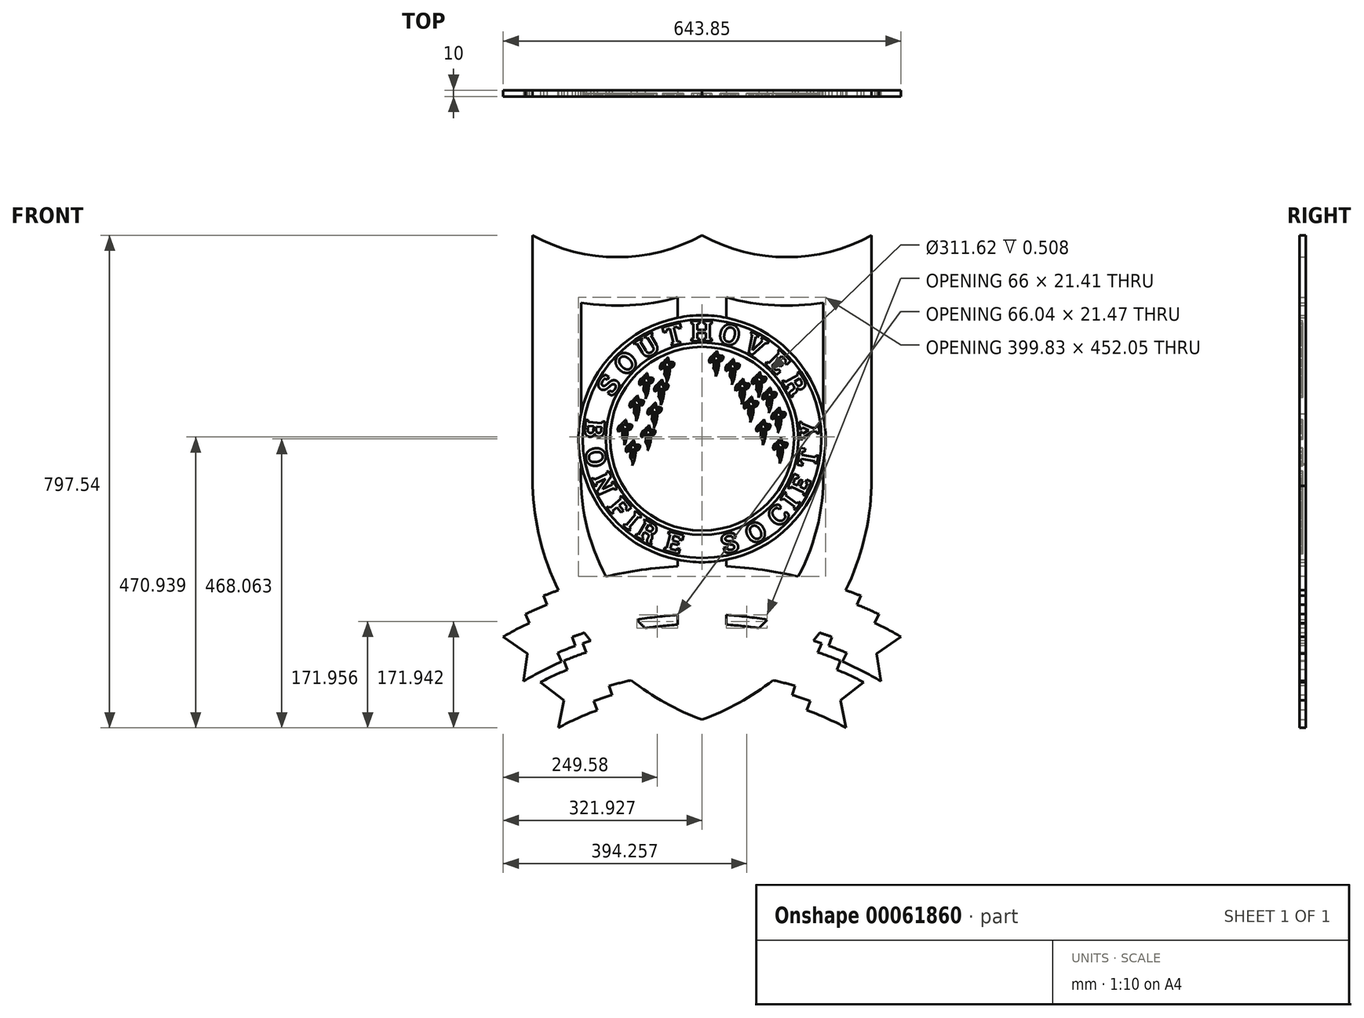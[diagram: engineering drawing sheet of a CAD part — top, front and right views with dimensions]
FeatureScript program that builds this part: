
annotation { "Feature Type Name" : "Feature", "Feature Type Description" : "" }
export const myFeature = defineFeature(function(context is Context, id is Id, definition is map)
    precondition{}
    {
        {
            var Q0;
            Q0=qCreatedBy(makeId("Front.planeOp"),FACE);
            var sketch = newSketch(context, id + "F0", { "sketchPlane" : qUnion([Q0])});
            skCircle(sketch, "E0", {"center": v(6.77, 469.76) * mm, "radius": 199.91 * mm});
            skSolve(sketch);
        }
        {
            var Q0;
            Q0 = qSketchRegion(id + "F0", true);
            extrude(context, id + "F1", {"entities" : qUnion([Q0]), "depth" : 10 * mm, "offsetDistance" : 25.4 * mm});
        }
        {
            var Q0;
            Q0=qCreatedBy(makeId("Front.planeOp"),FACE);
            var sketch = newSketch(context, id + "F2", { "sketchPlane" : qUnion([Q0])});
            skArc(sketch, "E1", {"start": v(-267.62, 799.24) * mm, "mid": v(-130.38, 764) * mm, "end": v(6.86, 799.22) * mm});
            skArc(sketch, "E2", {"start": v(-189.02, 690.2) * mm, "mid": v(-110.33, 685.87) * mm, "end": v(-32.56, 698.67) * mm});
            skArc(sketch, "E3", {"start": v(-189.02, 427.97) * mm, "mid": v(-152.25, 253.46) * mm, "end": v(-32.56, 121.24) * mm});
            skArc(sketch, "E4.0", {"start": v(-189.02, 510.16) * mm, "mid": v(-193.15, 469.76) * mm, "end": v(-189.02, 429.36) * mm});
            skLineSegment(sketch, "E5", {"start": v(6.77, 469.76) * mm, "end": v(-343.44, 469.76) * mm, "construction": true});
            skLineSegment(sketch, "E6", {"start": v(-343.44, 469.76) * mm, "end": v(6.77, -66.3) * mm, "construction": true});
            skLineSegment(sketch, "E7", {"start": v(6.77, -66.3) * mm, "end": v(6.77, 469.76) * mm, "construction": true});
            skLineSegment(sketch, "E8", {"start": v(-267.62, 799.24) * mm, "end": v(-267.62, 393.65) * mm});
            skArc(sketch, "E9", {"start": v(-267.62, 393.65) * mm, "mid": v(-188.5, 162.16) * mm, "end": v(6.77, 14.8) * mm});
            skLineSegment(sketch, "E10", {"start": v(-32.56, 698.67) * mm, "end": v(-32.56, 665.77) * mm});
            skLineSegment(sketch, "E11", {"start": v(-189.02, 690.2) * mm, "end": v(-189.02, 510.16) * mm});
            skArc(sketch, "E12.MirrorCS", {"start": v(281.15, 799.24) * mm, "mid": v(143.92, 764) * mm, "end": v(6.68, 799.22) * mm});
            skLineSegment(sketch, "E13.MirrorCS", {"start": v(281.15, 799.24) * mm, "end": v(281.15, 393.65) * mm});
            skArc(sketch, "E14.MirrorCS", {"start": v(202.56, 690.2) * mm, "mid": v(123.86, 685.87) * mm, "end": v(46.1, 698.67) * mm});
            skLineSegment(sketch, "E15.MirrorCS", {"start": v(202.56, 690.2) * mm, "end": v(202.56, 510.16) * mm});
            skLineSegment(sketch, "E16.MirrorCS", {"start": v(46.1, 698.67) * mm, "end": v(46.1, 665.77) * mm});
            skArc(sketch, "E17.MirrorCS", {"start": v(202.56, 427.97) * mm, "mid": v(165.79, 253.46) * mm, "end": v(46.1, 121.24) * mm});
            skArc(sketch, "E18.MirrorCS", {"start": v(281.15, 393.65) * mm, "mid": v(202.03, 162.16) * mm, "end": v(6.77, 14.8) * mm});
            skLineSegment(sketch, "E19.trimOffspring", {"start": v(-32.56, 273.76) * mm, "end": v(-32.56, 121.24) * mm});
            skLineSegment(sketch, "E20.trimOffspring", {"start": v(-189.02, 429.36) * mm, "end": v(-189.02, 427.97) * mm});
            skArc(sketch, "E21.trimOffspring", {"start": v(-32.56, 273.76) * mm, "mid": v(6.77, 269.85) * mm, "end": v(46.1, 273.76) * mm});
            skLineSegment(sketch, "E22.trimOffspring", {"start": v(46.1, 273.76) * mm, "end": v(46.1, 121.24) * mm});
            skArc(sketch, "E23.trimOffspring", {"start": v(202.56, 429.36) * mm, "mid": v(206.68, 469.76) * mm, "end": v(202.56, 510.16) * mm});
            skLineSegment(sketch, "E24.trimOffspring", {"start": v(202.56, 429.36) * mm, "end": v(202.56, 427.97) * mm});
            skArc(sketch, "E25.trimOffspring", {"start": v(46.1, 665.77) * mm, "mid": v(6.77, 669.68) * mm, "end": v(-32.56, 665.77) * mm});
            skSolve(sketch);
        }
        {
            var Q0;
            Q0 = qSketchRegion(id + "F2", true);
            extrude(context, id + "F3", {"entities" : qUnion([Q0]), "depth" : 10 * mm, "offsetDistance" : 25.4 * mm});
        }
        {
            var Q0;
            Q0=makeQuery(id+"F3.opExtrude","CAP_FACE",FACE,{"disambiguationData":[OSD([sQuery(id+"F2.wireOp",EDGE,"E1"),sQuery(id+"F2.wireOp",EDGE,"E2"),sQuery(id+"F2.wireOp",EDGE,"E3"),sQuery(id+"F2.wireOp",EDGE,"E8"),sQuery(id+"F2.wireOp",EDGE,"E9"),sQuery(id+"F2.wireOp",EDGE,"E10"),sQuery(id+"F2.wireOp",EDGE,"E11"),sQuery(id+"F2.wireOp",EDGE,"E12.MirrorCS"),sQuery(id+"F2.wireOp",EDGE,"E13.MirrorCS"),sQuery(id+"F2.wireOp",EDGE,"E14.MirrorCS"),sQuery(id+"F2.wireOp",EDGE,"E15.MirrorCS"),sQuery(id+"F2.wireOp",EDGE,"E16.MirrorCS"),sQuery(id+"F2.wireOp",EDGE,"E17.MirrorCS"),sQuery(id+"F2.wireOp",EDGE,"E18.MirrorCS")])],"isStart":false});
            var sketch = newSketch(context, id + "F4", { "sketchPlane" : qUnion([Q0])});
            skCircle(sketch, "E26.0", {"center": v(6.77, 469.76) * mm, "radius": 199.91 * mm, "construction": true});
            skLineSegment(sketch, "E27", {"start": v(6.77, 469.76) * mm, "end": v(6.77, 811.35) * mm, "construction": true});
            skArc(sketch, "E28", {"start": v(-8.6, 766.76) * mm, "mid": v(-16.65, 759.4) * mm, "end": v(-8.5, 752.14) * mm});
            skArc(sketch, "E29", {"start": v(-4.77, 746.9) * mm, "mid": v(-8.07, 738.78) * mm, "end": v(0.3, 736.11) * mm});
            skArc(sketch, "E30", {"start": v(2.95, 733.33) * mm, "mid": v(2.82, 728.75) * mm, "end": v(6.77, 726.42) * mm});
            skArc(sketch, "E31", {"start": v(-9.15, 782.05) * mm, "mid": v(-13.27, 776.66) * mm, "end": v(-8.73, 771.63) * mm});
            skArc(sketch, "E32", {"start": v(-9.15, 782.05) * mm, "mid": v(1.37, 788.5) * mm, "end": v(5.88, 800) * mm});
            skArc(sketch, "E33", {"start": v(2.95, 733.33) * mm, "mid": v(2.7, 735.76) * mm, "end": v(0.3, 736.11) * mm});
            skArc(sketch, "E34", {"start": v(-4.77, 746.9) * mm, "mid": v(-3.83, 747.3) * mm, "end": v(-2.92, 747.75) * mm});
            skArc(sketch, "E35", {"start": v(-8.5, 752.14) * mm, "mid": v(-6.95, 752.43) * mm, "end": v(-5.47, 752.96) * mm});
            skArc(sketch, "E36", {"start": v(-8.6, 766.76) * mm, "mid": v(-7.07, 766.64) * mm, "end": v(-5.54, 766.59) * mm});
            skArc(sketch, "E37", {"start": v(-8.73, 771.63) * mm, "mid": v(-7.17, 771.47) * mm, "end": v(-5.61, 771.46) * mm});
            skArc(sketch, "E38", {"start": v(-2.92, 747.75) * mm, "mid": v(-1.7, 751.58) * mm, "end": v(-5.47, 752.96) * mm});
            skArc(sketch, "E39", {"start": v(-5.54, 766.59) * mm, "mid": v(-3.07, 769.06) * mm, "end": v(-5.61, 771.46) * mm});
            skArc(sketch, "E40.0", {"start": v(-8.76, 780.32) * mm, "mid": v(0.95, 785.48) * mm, "end": v(6.77, 794.8) * mm});
            skLineSegment(sketch, "E41.0", {"start": v(7.66, 800) * mm, "end": v(5.88, 800) * mm});
            skPoint(sketch, "E42.orphan", {"position": v(-268.66, 800) * mm});
            skPoint(sketch, "E43.orphan", {"position": v(282.43, 800) * mm});
            skArc(sketch, "E44.0", {"start": v(-8.47, 773.39) * mm, "mid": v(-7.08, 773.25) * mm, "end": v(-5.68, 773.24) * mm});
            skArc(sketch, "E44.1", {"start": v(-5.57, 764.81) * mm, "mid": v(-1.3, 769.08) * mm, "end": v(-5.68, 773.24) * mm});
            skArc(sketch, "E44.2", {"start": v(-8.76, 764.99) * mm, "mid": v(-7.17, 764.86) * mm, "end": v(-5.57, 764.81) * mm});
            skArc(sketch, "E45.0", {"start": v(-5.54, 744.78) * mm, "mid": v(-3.76, 745.39) * mm, "end": v(-2.07, 746.19) * mm});
            skArc(sketch, "E45.1", {"start": v(-2.07, 746.19) * mm, "mid": v(-0.1, 752.36) * mm, "end": v(-6.19, 754.58) * mm});
            skArc(sketch, "E45.2", {"start": v(-8.7, 753.91) * mm, "mid": v(-7.42, 754.15) * mm, "end": v(-6.19, 754.58) * mm});
            skArc(sketch, "E46.0", {"start": v(4.46, 732.38) * mm, "mid": v(4, 736.99) * mm, "end": v(-0.59, 737.66) * mm});
            skArc(sketch, "E47.0", {"start": v(4.46, 732.38) * mm, "mid": v(4.38, 729.6) * mm, "end": v(6.77, 728.2) * mm});
            skArc(sketch, "E48.0", {"start": v(-4.14, 745.24) * mm, "mid": v(-6.46, 739.53) * mm, "end": v(-0.59, 737.66) * mm});
            skArc(sketch, "E49.0", {"start": v(-8.76, 780.32) * mm, "mid": v(-11.5, 776.73) * mm, "end": v(-8.47, 773.39) * mm});
            skArc(sketch, "E50.0", {"start": v(-8.76, 764.99) * mm, "mid": v(-14.87, 759.4) * mm, "end": v(-8.7, 753.91) * mm});
            skLineSegment(sketch, "E51.MirrorCS", {"start": v(5.88, 800) * mm, "end": v(5.88, 800) * mm});
            skArc(sketch, "E52.MirrorCS", {"start": v(22.13, 766.76) * mm, "mid": v(20.6, 766.64) * mm, "end": v(19.08, 766.59) * mm});
            skArc(sketch, "E53.MirrorCS", {"start": v(22, 773.39) * mm, "mid": v(20.62, 773.25) * mm, "end": v(19.22, 773.24) * mm});
            skArc(sketch, "E54.MirrorCS", {"start": v(22.03, 752.14) * mm, "mid": v(20.49, 752.43) * mm, "end": v(19, 752.96) * mm});
            skArc(sketch, "E55.MirrorCS", {"start": v(22.3, 764.99) * mm, "mid": v(20.7, 764.86) * mm, "end": v(19.1, 764.81) * mm});
            skArc(sketch, "E56.MirrorCS", {"start": v(18.3, 746.9) * mm, "mid": v(17.36, 747.3) * mm, "end": v(16.45, 747.75) * mm});
            skArc(sketch, "E57.MirrorCS", {"start": v(22.23, 753.91) * mm, "mid": v(20.95, 754.15) * mm, "end": v(19.72, 754.58) * mm});
            skArc(sketch, "E58.MirrorCS", {"start": v(22.26, 771.63) * mm, "mid": v(20.7, 771.47) * mm, "end": v(19.15, 771.46) * mm});
            skArc(sketch, "E59.MirrorCS", {"start": v(9.08, 732.38) * mm, "mid": v(9.16, 729.6) * mm, "end": v(6.77, 728.2) * mm});
            skArc(sketch, "E60.MirrorCS", {"start": v(10.58, 733.33) * mm, "mid": v(10.83, 735.76) * mm, "end": v(13.24, 736.11) * mm});
            skArc(sketch, "E61.MirrorCS", {"start": v(19.07, 744.78) * mm, "mid": v(17.3, 745.39) * mm, "end": v(15.6, 746.19) * mm});
            skArc(sketch, "E62.MirrorCS", {"start": v(19.08, 766.59) * mm, "mid": v(16.6, 769.06) * mm, "end": v(19.15, 771.46) * mm});
            skArc(sketch, "E63.MirrorCS", {"start": v(22.3, 780.32) * mm, "mid": v(12.58, 785.48) * mm, "end": v(6.77, 794.8) * mm});
            skArc(sketch, "E64.MirrorCS", {"start": v(16.45, 747.75) * mm, "mid": v(15.24, 751.58) * mm, "end": v(19, 752.96) * mm});
            skArc(sketch, "E65.MirrorCS", {"start": v(9.08, 732.38) * mm, "mid": v(9.54, 736.99) * mm, "end": v(14.12, 737.66) * mm});
            skArc(sketch, "E66.MirrorCS", {"start": v(22.3, 764.99) * mm, "mid": v(28.4, 759.4) * mm, "end": v(22.23, 753.91) * mm});
            skArc(sketch, "E67.MirrorCS", {"start": v(22.69, 782.05) * mm, "mid": v(12.16, 788.5) * mm, "end": v(7.66, 800) * mm});
            skArc(sketch, "E68.MirrorCS", {"start": v(10.58, 733.33) * mm, "mid": v(10.71, 728.75) * mm, "end": v(6.77, 726.42) * mm});
            skArc(sketch, "E69.MirrorCS", {"start": v(17.67, 745.24) * mm, "mid": v(20, 739.53) * mm, "end": v(14.12, 737.66) * mm});
            skArc(sketch, "E70.MirrorCS", {"start": v(18.3, 746.9) * mm, "mid": v(21.6, 738.78) * mm, "end": v(13.24, 736.11) * mm});
            skArc(sketch, "E71.MirrorCS", {"start": v(22.69, 782.05) * mm, "mid": v(26.8, 776.66) * mm, "end": v(22.26, 771.63) * mm});
            skArc(sketch, "E72.MirrorCS", {"start": v(22.13, 766.76) * mm, "mid": v(30.18, 759.4) * mm, "end": v(22.03, 752.14) * mm});
            skArc(sketch, "E73.MirrorCS", {"start": v(22.3, 780.32) * mm, "mid": v(25.03, 776.73) * mm, "end": v(22, 773.39) * mm});
            skArc(sketch, "E74.MirrorCS", {"start": v(19.1, 764.81) * mm, "mid": v(14.83, 769.08) * mm, "end": v(19.22, 773.24) * mm});
            skArc(sketch, "E75.MirrorCS", {"start": v(15.6, 746.19) * mm, "mid": v(13.64, 752.36) * mm, "end": v(19.72, 754.58) * mm});
            skArc(sketch, "E76.trimOffspring", {"start": v(5.88, 799.98) * mm, "mid": v(5.88, 799.99) * mm, "end": v(5.88, 800) * mm});
            skArc(sketch, "E77.trimOffspring", {"start": v(7.66, 799.98) * mm, "mid": v(7.66, 799.99) * mm, "end": v(7.66, 800) * mm});
            skArc(sketch, "E78", {"start": v(6.77, 739.23) * mm, "mid": v(7.13, 743.58) * mm, "end": v(7.42, 747.94) * mm});
            skArc(sketch, "E79", {"start": v(6.99, 782.56) * mm, "mid": v(13.75, 778.46) * mm, "end": v(21.5, 776.88) * mm});
            skArc(sketch, "E80", {"start": v(7.12, 780.88) * mm, "mid": v(13.95, 777.58) * mm, "end": v(21.5, 776.88) * mm});
            skArc(sketch, "E81", {"start": v(7.82, 764.42) * mm, "mid": v(14.94, 760.75) * mm, "end": v(22.84, 759.45) * mm});
            skArc(sketch, "E82", {"start": v(7.83, 762.95) * mm, "mid": v(15.05, 759.97) * mm, "end": v(22.84, 759.45) * mm});
            skArc(sketch, "E83", {"start": v(7.49, 749.17) * mm, "mid": v(10.93, 744.23) * mm, "end": v(16.2, 741.31) * mm});
            skArc(sketch, "E84", {"start": v(7.42, 747.94) * mm, "mid": v(10.85, 743.37) * mm, "end": v(16.2, 741.31) * mm});
            skPoint(sketch, "E85.MirrorCS.end.orphan", {"position": v(6.77, 785.08) * mm});
            skPoint(sketch, "E85.MirrorCS.start.orphan", {"position": v(6.77, 739.23) * mm});
            skArc(sketch, "E86.trimOffspring", {"start": v(6.99, 782.56) * mm, "mid": v(6.88, 783.82) * mm, "end": v(6.77, 785.08) * mm});
            skArc(sketch, "E87.trimOffspring", {"start": v(7.82, 764.42) * mm, "mid": v(7.6, 772.66) * mm, "end": v(7.12, 780.88) * mm});
            skArc(sketch, "E88.trimOffspring", {"start": v(7.49, 749.17) * mm, "mid": v(7.75, 756.06) * mm, "end": v(7.83, 762.95) * mm});
            skArc(sketch, "E89.MirrorCS", {"start": v(6.55, 782.56) * mm, "mid": v(-0.22, 778.46) * mm, "end": v(-7.97, 776.88) * mm});
            skArc(sketch, "E90.MirrorCS", {"start": v(6.41, 780.88) * mm, "mid": v(-0.41, 777.58) * mm, "end": v(-7.97, 776.88) * mm});
            skArc(sketch, "E91.MirrorCS", {"start": v(5.72, 764.42) * mm, "mid": v(5.93, 772.66) * mm, "end": v(6.41, 780.88) * mm});
            skArc(sketch, "E92.MirrorCS", {"start": v(6.55, 782.56) * mm, "mid": v(6.65, 783.82) * mm, "end": v(6.77, 785.08) * mm});
            skArc(sketch, "E93.MirrorCS", {"start": v(5.7, 762.95) * mm, "mid": v(-1.51, 759.97) * mm, "end": v(-9.3, 759.45) * mm});
            skArc(sketch, "E94.MirrorCS", {"start": v(6.05, 749.17) * mm, "mid": v(5.78, 756.06) * mm, "end": v(5.7, 762.95) * mm});
            skArc(sketch, "E95.MirrorCS", {"start": v(5.72, 764.42) * mm, "mid": v(-1.4, 760.75) * mm, "end": v(-9.3, 759.45) * mm});
            skArc(sketch, "E96.MirrorCS", {"start": v(6.05, 749.17) * mm, "mid": v(2.6, 744.23) * mm, "end": v(-2.66, 741.31) * mm});
            skArc(sketch, "E97.MirrorCS", {"start": v(6.11, 747.94) * mm, "mid": v(2.68, 743.37) * mm, "end": v(-2.66, 741.31) * mm});
            skArc(sketch, "E98.MirrorCS", {"start": v(6.77, 739.23) * mm, "mid": v(6.4, 743.58) * mm, "end": v(6.11, 747.94) * mm});
            skSolve(sketch);
        }
        {
            var Q0;
            {var subQ151=sQuery(id+"F2.wireOp",EDGE,"E1");var subQ170=sQuery(id+"F2.wireOp",EDGE,"E12.MirrorCS");var subQ178=makeQuery(id+"F3.opExtrude","SWEPT_FACE",FACE,{"disambiguationData":[OSD([subQ151])]});var subQ182=sQuery(id+"F2.wireOp",EDGE,"E9");var subQ204=sQuery(id+"F2.wireOp",EDGE,"E3");var subQ205=makeQuery(id+"F3.opExtrude","SWEPT_FACE",FACE,{"disambiguationData":[OSD([subQ204])]});var subQ208=sQuery(id+"F2.wireOp",EDGE,"E2");var subQ209=makeQuery(id+"F3.opExtrude","SWEPT_FACE",FACE,{"disambiguationData":[OSD([subQ208])]});var subQ210=sQuery(id+"F2.wireOp",EDGE,"E10");var subQ568=sQuery(id+"F2.wireOp",EDGE,"E16.MirrorCS");var subQ570=sQuery(id+"F2.wireOp",EDGE,"E17.MirrorCS");var subQ572=sQuery(id+"F2.wireOp",EDGE,"E18.MirrorCS");var subQ581=sQuery(id+"F2.wireOp",EDGE,"E14.MirrorCS");var subQ871=sQuery(id+"F2.wireOp",EDGE,"E15.MirrorCS");var subQ872=sQuery(id+"F2.wireOp",EDGE,"E13.MirrorCS");var subQ873=sQuery(id+"F2.wireOp",EDGE,"E11");var subQ874=sQuery(id+"F2.wireOp",EDGE,"E8");var subQ875=makeQuery(id+"F3.opExtrude","CAP_FACE",FACE,{"disambiguationData":[OSD([subQ151,subQ208,subQ204,subQ874,subQ182,subQ210,subQ873,subQ170,subQ872,subQ581,subQ871,subQ568,subQ570,subQ572])],"isStart":false});Q0=makeQuery(id+"FD2YuUjZby6Q1ET_2.1_10.FR0OegjQK6V7KqL_2.boolean.opBoolean","SPLIT",FACE,{"disambiguationData":[TD([subQ178])],"derivedFrom":makeQuery(id+"FD2YuUjZby6Q1ET_2.0_10.FR0OegjQK6V7KqL_2.boolean.opBoolean","SPLIT",FACE,{"disambiguationData":[TD([subQ178])],"derivedFrom":makeQuery(id+"FD2YuUjZby6Q1ET_2.-1_10.FR0OegjQK6V7KqL_2.boolean.opBoolean","SPLIT",FACE,{"disambiguationData":[TD([subQ178])],"derivedFrom":makeQuery(id+"FD2YuUjZby6Q1ET_2.2_9.FR0OegjQK6V7KqL_2.boolean.opBoolean","SPLIT",FACE,{"disambiguationData":[TD([subQ178])],"derivedFrom":makeQuery(id+"FD2YuUjZby6Q1ET_2.1_9.FR0OegjQK6V7KqL_2.boolean.opBoolean","SPLIT",FACE,{"disambiguationData":[TD([subQ178])],"derivedFrom":makeQuery(id+"FD2YuUjZby6Q1ET_2.0_9.FR0OegjQK6V7KqL_2.boolean.opBoolean","SPLIT",FACE,{"disambiguationData":[TD([subQ178])],"derivedFrom":makeQuery(id+"FD2YuUjZby6Q1ET_2.-1_9.FR0OegjQK6V7KqL_2.boolean.opBoolean","SPLIT",FACE,{"disambiguationData":[TD([subQ178])],"derivedFrom":makeQuery(id+"FD2YuUjZby6Q1ET_2.-2_9.FR0OegjQK6V7KqL_2.boolean.opBoolean","SPLIT",FACE,{"disambiguationData":[TD([subQ178])],"derivedFrom":makeQuery(id+"FD2YuUjZby6Q1ET_2.3_8.FR0OegjQK6V7KqL_2.boolean.opBoolean","SPLIT",FACE,{"disambiguationData":[TD([subQ209])],"derivedFrom":makeQuery(id+"FD2YuUjZby6Q1ET_2.2_8.FR0OegjQK6V7KqL_2.boolean.opBoolean","SPLIT",FACE,{"disambiguationData":[TD([subQ178])],"derivedFrom":makeQuery(id+"FD2YuUjZby6Q1ET_2.0_8.FR0OegjQK6V7KqL_2.boolean.opBoolean","SPLIT",FACE,{"disambiguationData":[TD([subQ178])],"derivedFrom":makeQuery(id+"FD2YuUjZby6Q1ET_2.-2_8.FR0OegjQK6V7KqL_2.boolean.opBoolean","SPLIT",FACE,{"disambiguationData":[TD([subQ178])],"derivedFrom":makeQuery(id+"FD2YuUjZby6Q1ET_2.-3_8.FR0OegjQK6V7KqL_2.boolean.opBoolean","SPLIT",FACE,{"disambiguationData":[TD([subQ178])],"derivedFrom":makeQuery(id+"FD2YuUjZby6Q1ET_2.4_7.FR0OegjQK6V7KqL_2.boolean.opBoolean","SPLIT",FACE,{"disambiguationData":[TD([subQ178])],"derivedFrom":makeQuery(id+"FD2YuUjZby6Q1ET_2.3_7.FR0OegjQK6V7KqL_2.boolean.opBoolean","SPLIT",FACE,{"disambiguationData":[TD([subQ178])],"derivedFrom":makeQuery(id+"FD2YuUjZby6Q1ET_2.0_7.FR0OegjQK6V7KqL_2.boolean.opBoolean","SPLIT",FACE,{"disambiguationData":[TD([subQ178])],"derivedFrom":makeQuery(id+"FD2YuUjZby6Q1ET_2.-3_7.FR0OegjQK6V7KqL_2.boolean.opBoolean","SPLIT",FACE,{"disambiguationData":[TD([subQ178])],"derivedFrom":makeQuery(id+"FD2YuUjZby6Q1ET_2.-4_7.FR0OegjQK6V7KqL_2.boolean.opBoolean","SPLIT",FACE,{"disambiguationData":[TD([subQ178])],"derivedFrom":makeQuery(id+"FD2YuUjZby6Q1ET_2.4_6.FR0OegjQK6V7KqL_2.boolean.opBoolean","SPLIT",FACE,{"disambiguationData":[TD([subQ209])],"derivedFrom":makeQuery(id+"FD2YuUjZby6Q1ET_2.3_6.FR0OegjQK6V7KqL_2.boolean.opBoolean","SPLIT",FACE,{"disambiguationData":[TD([subQ178])],"derivedFrom":makeQuery(id+"FD2YuUjZby6Q1ET_2.0_6.FR0OegjQK6V7KqL_2.boolean.opBoolean","SPLIT",FACE,{"disambiguationData":[TD([subQ178])],"derivedFrom":makeQuery(id+"FD2YuUjZby6Q1ET_2.-3_6.FR0OegjQK6V7KqL_2.boolean.opBoolean","SPLIT",FACE,{"disambiguationData":[TD([subQ178])],"derivedFrom":makeQuery(id+"FD2YuUjZby6Q1ET_2.-4_6.FR0OegjQK6V7KqL_2.boolean.opBoolean","SPLIT",FACE,{"disambiguationData":[TD([subQ178])],"derivedFrom":makeQuery(id+"FD2YuUjZby6Q1ET_2.4_5.FR0OegjQK6V7KqL_2.boolean.opBoolean","SPLIT",FACE,{"disambiguationData":[TD([subQ178])],"derivedFrom":makeQuery(id+"FD2YuUjZby6Q1ET_2.3_5.FR0OegjQK6V7KqL_2.boolean.opBoolean","SPLIT",FACE,{"disambiguationData":[TD([subQ178])],"derivedFrom":makeQuery(id+"FD2YuUjZby6Q1ET_2.0_5.FR0OegjQK6V7KqL_2.boolean.opBoolean","SPLIT",FACE,{"disambiguationData":[TD([subQ178])],"derivedFrom":makeQuery(id+"FD2YuUjZby6Q1ET_2.-3_5.FR0OegjQK6V7KqL_2.boolean.opBoolean","SPLIT",FACE,{"disambiguationData":[TD([subQ178])],"derivedFrom":makeQuery(id+"FD2YuUjZby6Q1ET_2.-4_5.FR0OegjQK6V7KqL_2.boolean.opBoolean","SPLIT",FACE,{"disambiguationData":[TD([subQ178])],"derivedFrom":makeQuery(id+"FD2YuUjZby6Q1ET_2.4_4.FR0OegjQK6V7KqL_2.boolean.opBoolean","SPLIT",FACE,{"disambiguationData":[TD([subQ178])],"derivedFrom":makeQuery(id+"FD2YuUjZby6Q1ET_2.3_4.FR0OegjQK6V7KqL_2.boolean.opBoolean","SPLIT",FACE,{"disambiguationData":[TD([subQ178])],"derivedFrom":makeQuery(id+"FD2YuUjZby6Q1ET_2.0_4.FR0OegjQK6V7KqL_2.boolean.opBoolean","SPLIT",FACE,{"disambiguationData":[TD([subQ178])],"derivedFrom":makeQuery(id+"FD2YuUjZby6Q1ET_2.-3_4.FR0OegjQK6V7KqL_2.boolean.opBoolean","SPLIT",FACE,{"disambiguationData":[TD([subQ178])],"derivedFrom":makeQuery(id+"FD2YuUjZby6Q1ET_2.-4_4.FR0OegjQK6V7KqL_2.boolean.opBoolean","SPLIT",FACE,{"disambiguationData":[TD([subQ178])],"derivedFrom":makeQuery(id+"FD2YuUjZby6Q1ET_2.4_3.FR0OegjQK6V7KqL_2.boolean.opBoolean","SPLIT",FACE,{"disambiguationData":[TD([subQ178])],"derivedFrom":makeQuery(id+"FD2YuUjZby6Q1ET_2.3_3.FR0OegjQK6V7KqL_2.boolean.opBoolean","SPLIT",FACE,{"disambiguationData":[TD([subQ178])],"derivedFrom":makeQuery(id+"FD2YuUjZby6Q1ET_2.0_3.FR0OegjQK6V7KqL_2.boolean.opBoolean","SPLIT",FACE,{"disambiguationData":[TD([subQ178])],"derivedFrom":makeQuery(id+"FD2YuUjZby6Q1ET_2.-3_3.FR0OegjQK6V7KqL_2.boolean.opBoolean","SPLIT",FACE,{"disambiguationData":[TD([subQ178])],"derivedFrom":makeQuery(id+"FD2YuUjZby6Q1ET_2.-4_3.FR0OegjQK6V7KqL_2.boolean.opBoolean","SPLIT",FACE,{"disambiguationData":[TD([subQ178])],"derivedFrom":makeQuery(id+"FD2YuUjZby6Q1ET_2.4_2.FR0OegjQK6V7KqL_2.boolean.opBoolean","SPLIT",FACE,{"disambiguationData":[TD([subQ178])],"derivedFrom":makeQuery(id+"FD2YuUjZby6Q1ET_2.3_2.FR0OegjQK6V7KqL_2.boolean.opBoolean","SPLIT",FACE,{"disambiguationData":[TD([subQ178])],"derivedFrom":makeQuery(id+"FD2YuUjZby6Q1ET_2.0_2.FR0OegjQK6V7KqL_2.boolean.opBoolean","SPLIT",FACE,{"disambiguationData":[TD([subQ178])],"derivedFrom":makeQuery(id+"FD2YuUjZby6Q1ET_2.-3_2.FR0OegjQK6V7KqL_2.boolean.opBoolean","SPLIT",FACE,{"disambiguationData":[TD([subQ178])],"derivedFrom":makeQuery(id+"FD2YuUjZby6Q1ET_2.-4_2.FR0OegjQK6V7KqL_2.boolean.opBoolean","SPLIT",FACE,{"disambiguationData":[TD([subQ178])],"derivedFrom":makeQuery(id+"FD2YuUjZby6Q1ET_2.4_1.FR0OegjQK6V7KqL_2.boolean.opBoolean","SPLIT",FACE,{"disambiguationData":[TD([subQ178])],"derivedFrom":makeQuery(id+"FD2YuUjZby6Q1ET_2.3_1.FR0OegjQK6V7KqL_2.boolean.opBoolean","SPLIT",FACE,{"disambiguationData":[TD([subQ205])],"derivedFrom":makeQuery(id+"FD2YuUjZby6Q1ET_2.2_1.FR0OegjQK6V7KqL_2.boolean.opBoolean","SPLIT",FACE,{"disambiguationData":[TD([subQ205])],"derivedFrom":makeQuery(id+"FD2YuUjZby6Q1ET_2.1_1.FR0OegjQK6V7KqL_2.boolean.opBoolean","SPLIT",FACE,{"disambiguationData":[TD([subQ178])],"derivedFrom":makeQuery(id+"FD2YuUjZby6Q1ET_2.0_1.FR0OegjQK6V7KqL_2.boolean.opBoolean","SPLIT",FACE,{"disambiguationData":[TD([subQ178])],"derivedFrom":makeQuery(id+"FD2YuUjZby6Q1ET_2.-1_1.FR0OegjQK6V7KqL_2.boolean.opBoolean","SPLIT",FACE,{"disambiguationData":[TD([subQ178])],"derivedFrom":makeQuery(id+"FD2YuUjZby6Q1ET_2.-2_1.FR0OegjQK6V7KqL_2.boolean.opBoolean","SPLIT",FACE,{"disambiguationData":[TD([subQ178])],"derivedFrom":makeQuery(id+"FD2YuUjZby6Q1ET_2.-3_1.FR0OegjQK6V7KqL_2.boolean.opBoolean","SPLIT",FACE,{"disambiguationData":[TD([subQ178])],"derivedFrom":makeQuery(id+"FD2YuUjZby6Q1ET_2.-4_1.FR0OegjQK6V7KqL_2.boolean.opBoolean","SPLIT",FACE,{"disambiguationData":[TD([subQ178])],"derivedFrom":makeQuery(id+"FD2YuUjZby6Q1ET_2.4.FR0OegjQK6V7KqL_2.boolean.opBoolean","SPLIT",FACE,{"disambiguationData":[TD([subQ209])],"derivedFrom":makeQuery(id+"FD2YuUjZby6Q1ET_2.3.FR0OegjQK6V7KqL_2.boolean.opBoolean","SPLIT",FACE,{"disambiguationData":[TD([subQ209])],"derivedFrom":makeQuery(id+"FD2YuUjZby6Q1ET_2.2.FR0OegjQK6V7KqL_2.boolean.opBoolean","SPLIT",FACE,{"disambiguationData":[TD([subQ209])],"derivedFrom":makeQuery(id+"FD2YuUjZby6Q1ET_2.1.FR0OegjQK6V7KqL_2.boolean.opBoolean","SPLIT",FACE,{"disambiguationData":[TD([subQ209])],"derivedFrom":makeQuery(id+"FD2YuUjZby6Q1ET_2.-1.FR0OegjQK6V7KqL_2.boolean.opBoolean","SPLIT",FACE,{"disambiguationData":[TD([subQ178])],"derivedFrom":makeQuery(id+"FD2YuUjZby6Q1ET_2.-2.FR0OegjQK6V7KqL_2.boolean.opBoolean","SPLIT",FACE,{"disambiguationData":[TD([subQ178])],"derivedFrom":makeQuery(id+"FD2YuUjZby6Q1ET_2.-3.FR0OegjQK6V7KqL_2.boolean.opBoolean","SPLIT",FACE,{"disambiguationData":[TD([subQ178])],"derivedFrom":makeQuery(id+"FD2YuUjZby6Q1ET_2.-4.FR0OegjQK6V7KqL_2.boolean.opBoolean","SPLIT",FACE,{"disambiguationData":[TD([subQ178])],"derivedFrom":makeQuery(id+"FR0OegjQK6V7KqL_2.boolean.opBoolean","SPLIT",FACE,{"disambiguationData":[TD([subQ178])],"derivedFrom":subQ875})})})})})})})})})})})})})})})})})})})})})})})})})})})})})})})})})})})})})})})})})})})})})})})})})})})})})})})})})})})})});}
            var sketch = newSketch(context, id + "F5", { "sketchPlane" : qUnion([Q0])});
            skCircle(sketch, "E99.0", {"center": v(-24.28, 435.37) * mm, "radius": 199.91 * mm, "construction": true});
            skLineSegment(sketch, "E100", {"start": v(-24.28, 435.37) * mm, "end": v(-24.28, 776.96) * mm, "construction": true});
            skArc(sketch, "E101", {"start": v(-39.64, 732.36) * mm, "mid": v(-47.7, 725) * mm, "end": v(-39.54, 717.75) * mm});
            skArc(sketch, "E102", {"start": v(-35.81, 712.51) * mm, "mid": v(-37.73, 711.33) * mm, "end": v(-39.08, 709.53) * mm});
            skArc(sketch, "E103", {"start": v(-28.1, 698.93) * mm, "mid": v(-28.23, 694.35) * mm, "end": v(-24.28, 692.02) * mm});
            skArc(sketch, "E104", {"start": v(-40.2, 747.65) * mm, "mid": v(-41.55, 747.14) * mm, "end": v(-42.72, 746.28) * mm});
            skArc(sketch, "E105", {"start": v(-40.2, 747.65) * mm, "mid": v(-29.67, 754.1) * mm, "end": v(-25.17, 765.6) * mm});
            skArc(sketch, "E106", {"start": v(-28.1, 698.93) * mm, "mid": v(-28.34, 701.36) * mm, "end": v(-30.76, 701.72) * mm});
            skArc(sketch, "E107", {"start": v(-35.81, 712.51) * mm, "mid": v(-34.88, 712.9) * mm, "end": v(-33.97, 713.36) * mm});
            skArc(sketch, "E108", {"start": v(-39.54, 717.75) * mm, "mid": v(-38, 718.04) * mm, "end": v(-36.52, 718.56) * mm});
            skArc(sketch, "E109", {"start": v(-39.64, 732.36) * mm, "mid": v(-38.12, 732.24) * mm, "end": v(-36.6, 732.2) * mm});
            skArc(sketch, "E110", {"start": v(-39.78, 737.23) * mm, "mid": v(-38.22, 737.08) * mm, "end": v(-36.66, 737.07) * mm});
            skArc(sketch, "E111", {"start": v(-33.97, 713.36) * mm, "mid": v(-32.75, 717.18) * mm, "end": v(-36.52, 718.56) * mm});
            skArc(sketch, "E112", {"start": v(-36.6, 732.2) * mm, "mid": v(-34.12, 734.66) * mm, "end": v(-36.66, 737.07) * mm});
            skArc(sketch, "E113.0", {"start": v(-39.8, 745.92) * mm, "mid": v(-30.1, 751.08) * mm, "end": v(-24.28, 760.41) * mm});
            skLineSegment(sketch, "E114.0", {"start": v(-23.39, 765.6) * mm, "end": v(-25.17, 765.6) * mm});
            skPoint(sketch, "E115.orphan", {"position": v(-299.71, 765.6) * mm});
            skPoint(sketch, "E116.orphan", {"position": v(251.39, 765.6) * mm});
            skArc(sketch, "E117.0", {"start": v(-39.52, 739) * mm, "mid": v(-38.13, 738.85) * mm, "end": v(-36.73, 738.85) * mm});
            skArc(sketch, "E117.1", {"start": v(-36.62, 730.41) * mm, "mid": v(-32.34, 734.69) * mm, "end": v(-36.73, 738.85) * mm});
            skArc(sketch, "E117.2", {"start": v(-39.81, 730.6) * mm, "mid": v(-38.22, 730.47) * mm, "end": v(-36.62, 730.41) * mm});
            skArc(sketch, "E118.0", {"start": v(-35.19, 710.85) * mm, "mid": v(-34.14, 711.28) * mm, "end": v(-33.12, 711.8) * mm});
            skArc(sketch, "E118.1", {"start": v(-33.12, 711.8) * mm, "mid": v(-31.15, 717.97) * mm, "end": v(-37.24, 720.19) * mm});
            skArc(sketch, "E118.2", {"start": v(-39.74, 719.52) * mm, "mid": v(-38.46, 719.76) * mm, "end": v(-37.24, 720.19) * mm});
            skArc(sketch, "E119.0", {"start": v(-26.6, 697.99) * mm, "mid": v(-27.06, 702.6) * mm, "end": v(-31.63, 703.27) * mm});
            skArc(sketch, "E120.0", {"start": v(-26.6, 697.99) * mm, "mid": v(-26.67, 695.21) * mm, "end": v(-24.28, 693.8) * mm});
            skArc(sketch, "E121.0", {"start": v(-35.19, 710.85) * mm, "mid": v(-36.55, 710) * mm, "end": v(-37.5, 708.7) * mm});
            skArc(sketch, "E122.0", {"start": v(-39.8, 745.92) * mm, "mid": v(-40.66, 745.6) * mm, "end": v(-41.4, 745.08) * mm});
            skArc(sketch, "E123.0", {"start": v(-39.81, 730.6) * mm, "mid": v(-45.92, 725.01) * mm, "end": v(-39.74, 719.52) * mm});
            skLineSegment(sketch, "E124.MirrorCS", {"start": v(-25.17, 765.6) * mm, "end": v(-25.17, 765.6) * mm});
            skArc(sketch, "E125.MirrorCS", {"start": v(-8.92, 732.36) * mm, "mid": v(-10.44, 732.24) * mm, "end": v(-11.97, 732.2) * mm});
            skArc(sketch, "E126.MirrorCS", {"start": v(-9.04, 739) * mm, "mid": v(-10.43, 738.85) * mm, "end": v(-11.83, 738.85) * mm});
            skArc(sketch, "E127.MirrorCS", {"start": v(-9.02, 717.75) * mm, "mid": v(-10.56, 718.04) * mm, "end": v(-12.04, 718.56) * mm});
            skArc(sketch, "E128.MirrorCS", {"start": v(-8.75, 730.6) * mm, "mid": v(-10.34, 730.47) * mm, "end": v(-11.95, 730.41) * mm});
            skArc(sketch, "E129.MirrorCS", {"start": v(-12.75, 712.51) * mm, "mid": v(-13.68, 712.9) * mm, "end": v(-14.6, 713.36) * mm});
            skArc(sketch, "E130.MirrorCS", {"start": v(-8.82, 719.52) * mm, "mid": v(-10.1, 719.76) * mm, "end": v(-11.32, 720.19) * mm});
            skArc(sketch, "E131.MirrorCS", {"start": v(-8.79, 737.23) * mm, "mid": v(-10.34, 737.08) * mm, "end": v(-11.9, 737.07) * mm});
            skArc(sketch, "E132.MirrorCS", {"start": v(-21.97, 697.99) * mm, "mid": v(-21.89, 695.21) * mm, "end": v(-24.28, 693.8) * mm});
            skArc(sketch, "E133.MirrorCS", {"start": v(-20.46, 698.93) * mm, "mid": v(-20.22, 701.36) * mm, "end": v(-17.8, 701.72) * mm});
            skArc(sketch, "E134.MirrorCS", {"start": v(-13.37, 710.85) * mm, "mid": v(-14.42, 711.28) * mm, "end": v(-15.44, 711.8) * mm});
            skArc(sketch, "E135.MirrorCS", {"start": v(-11.97, 732.2) * mm, "mid": v(-14.44, 734.66) * mm, "end": v(-11.9, 737.07) * mm});
            skArc(sketch, "E136.MirrorCS", {"start": v(-8.76, 745.92) * mm, "mid": v(-18.47, 751.08) * mm, "end": v(-24.28, 760.41) * mm});
            skArc(sketch, "E137.MirrorCS", {"start": v(-14.6, 713.36) * mm, "mid": v(-15.81, 717.18) * mm, "end": v(-12.04, 718.56) * mm});
            skArc(sketch, "E138.MirrorCS", {"start": v(-21.97, 697.99) * mm, "mid": v(-21.5, 702.6) * mm, "end": v(-16.93, 703.27) * mm});
            skArc(sketch, "E139.MirrorCS", {"start": v(-8.75, 730.6) * mm, "mid": v(-2.64, 725.01) * mm, "end": v(-8.82, 719.52) * mm});
            skArc(sketch, "E140.MirrorCS", {"start": v(-8.36, 747.65) * mm, "mid": v(-18.89, 754.1) * mm, "end": v(-23.4, 765.6) * mm});
            skArc(sketch, "E141.MirrorCS", {"start": v(-20.46, 698.93) * mm, "mid": v(-20.33, 694.35) * mm, "end": v(-24.28, 692.02) * mm});
            skArc(sketch, "E142.MirrorCS", {"start": v(-13.37, 710.85) * mm, "mid": v(-12.04, 710.03) * mm, "end": v(-11.1, 708.78) * mm});
            skArc(sketch, "E143.MirrorCS", {"start": v(-12.75, 712.51) * mm, "mid": v(-10.84, 711.35) * mm, "end": v(-9.5, 709.57) * mm});
            skArc(sketch, "E144.MirrorCS", {"start": v(-8.36, 747.65) * mm, "mid": v(-7.04, 747.16) * mm, "end": v(-5.9, 746.33) * mm});
            skArc(sketch, "E145.MirrorCS", {"start": v(-8.92, 732.36) * mm, "mid": v(-0.86, 725) * mm, "end": v(-9.02, 717.75) * mm});
            skArc(sketch, "E146.MirrorCS", {"start": v(-8.76, 745.92) * mm, "mid": v(-7.95, 745.63) * mm, "end": v(-7.24, 745.15) * mm});
            skArc(sketch, "E147.MirrorCS", {"start": v(-11.95, 730.41) * mm, "mid": v(-16.22, 734.69) * mm, "end": v(-11.83, 738.85) * mm});
            skArc(sketch, "E148.MirrorCS", {"start": v(-15.44, 711.8) * mm, "mid": v(-17.4, 717.97) * mm, "end": v(-11.32, 720.19) * mm});
            skArc(sketch, "E149.trimOffspring", {"start": v(-25.17, 765.58) * mm, "mid": v(-25.17, 765.6) * mm, "end": v(-25.17, 765.6) * mm});
            skArc(sketch, "E150.trimOffspring", {"start": v(-23.4, 765.58) * mm, "mid": v(-23.39, 765.6) * mm, "end": v(-23.39, 765.6) * mm});
            skArc(sketch, "E151", {"start": v(-24.28, 704.83) * mm, "mid": v(-23.91, 709.19) * mm, "end": v(-23.63, 713.55) * mm});
            skArc(sketch, "E152", {"start": v(-24.06, 748.16) * mm, "mid": v(-17.3, 744.07) * mm, "end": v(-9.55, 742.48) * mm});
            skArc(sketch, "E153", {"start": v(-23.93, 746.49) * mm, "mid": v(-17.1, 743.18) * mm, "end": v(-9.55, 742.48) * mm});
            skArc(sketch, "E154", {"start": v(-23.23, 730.03) * mm, "mid": v(-16.11, 726.36) * mm, "end": v(-8.2, 725.05) * mm});
            skArc(sketch, "E155", {"start": v(-23.22, 728.56) * mm, "mid": v(-16, 725.58) * mm, "end": v(-8.2, 725.05) * mm});
            skArc(sketch, "E156", {"start": v(-23.56, 714.78) * mm, "mid": v(-20.12, 709.84) * mm, "end": v(-14.86, 706.92) * mm});
            skArc(sketch, "E157", {"start": v(-23.63, 713.55) * mm, "mid": v(-20.2, 708.97) * mm, "end": v(-14.86, 706.92) * mm});
            skPoint(sketch, "E158.MirrorCS.end.orphan", {"position": v(-24.28, 750.69) * mm});
            skPoint(sketch, "E158.MirrorCS.start.orphan", {"position": v(-24.28, 704.83) * mm});
            skArc(sketch, "E159.trimOffspring", {"start": v(-24.06, 748.16) * mm, "mid": v(-24.17, 749.42) * mm, "end": v(-24.28, 750.69) * mm});
            skArc(sketch, "E160.trimOffspring", {"start": v(-23.23, 730.03) * mm, "mid": v(-23.44, 738.26) * mm, "end": v(-23.93, 746.49) * mm});
            skArc(sketch, "E161.trimOffspring", {"start": v(-23.56, 714.78) * mm, "mid": v(-23.3, 721.67) * mm, "end": v(-23.22, 728.56) * mm});
            skArc(sketch, "E162.MirrorCS", {"start": v(-24.5, 748.16) * mm, "mid": v(-31.27, 744.07) * mm, "end": v(-39.01, 742.48) * mm});
            skArc(sketch, "E163.MirrorCS", {"start": v(-24.63, 746.49) * mm, "mid": v(-31.46, 743.18) * mm, "end": v(-39.01, 742.48) * mm});
            skArc(sketch, "E164.MirrorCS", {"start": v(-25.33, 730.03) * mm, "mid": v(-25.12, 738.26) * mm, "end": v(-24.63, 746.49) * mm});
            skArc(sketch, "E165.MirrorCS", {"start": v(-24.5, 748.16) * mm, "mid": v(-24.4, 749.42) * mm, "end": v(-24.28, 750.69) * mm});
            skArc(sketch, "E166.MirrorCS", {"start": v(-25.34, 728.56) * mm, "mid": v(-32.56, 725.58) * mm, "end": v(-40.35, 725.05) * mm});
            skArc(sketch, "E167.MirrorCS", {"start": v(-25, 714.78) * mm, "mid": v(-25.27, 721.67) * mm, "end": v(-25.34, 728.56) * mm});
            skArc(sketch, "E168.MirrorCS", {"start": v(-25.33, 730.03) * mm, "mid": v(-32.45, 726.36) * mm, "end": v(-40.35, 725.05) * mm});
            skArc(sketch, "E169.MirrorCS", {"start": v(-25, 714.78) * mm, "mid": v(-28.44, 709.84) * mm, "end": v(-33.7, 706.92) * mm});
            skArc(sketch, "E170.MirrorCS", {"start": v(-24.93, 713.55) * mm, "mid": v(-28.37, 708.97) * mm, "end": v(-33.7, 706.92) * mm});
            skArc(sketch, "E171.MirrorCS", {"start": v(-24.28, 704.83) * mm, "mid": v(-24.65, 709.19) * mm, "end": v(-24.93, 713.55) * mm});
            skArc(sketch, "E172.0", {"start": v(-42.72, 746.28) * mm, "mid": v(-42.01, 745.73) * mm, "end": v(-41.4, 745.08) * mm});
            skArc(sketch, "E173.0", {"start": v(-5.9, 746.33) * mm, "mid": v(-6.61, 745.8) * mm, "end": v(-7.24, 745.15) * mm});
            skArc(sketch, "E174.0", {"start": v(-39.08, 709.53) * mm, "mid": v(-38.26, 709.18) * mm, "end": v(-37.5, 708.7) * mm});
            skArc(sketch, "E175.0", {"start": v(-9.5, 709.57) * mm, "mid": v(-10.33, 709.24) * mm, "end": v(-11.1, 708.78) * mm});
            skArc(sketch, "E176.trimOffspring", {"start": v(-41.29, 737.69) * mm, "mid": v(-40.55, 737.4) * mm, "end": v(-39.78, 737.23) * mm});
            skArc(sketch, "E177.trimOffspring", {"start": v(-40.43, 739.25) * mm, "mid": v(-39.98, 739.09) * mm, "end": v(-39.52, 739) * mm});
            skPoint(sketch, "E178.orphan", {"position": v(-48.99, 736.11) * mm});
            skArc(sketch, "E179.trimOffspring", {"start": v(-40.43, 739.25) * mm, "mid": v(-40.8, 738.44) * mm, "end": v(-41.29, 737.69) * mm});
            skPoint(sketch, "E180.orphan", {"position": v(-43.93, 746.9) * mm});
            skArc(sketch, "E181.trimOffspring", {"start": v(-7.37, 737.64) * mm, "mid": v(-8.06, 737.39) * mm, "end": v(-8.79, 737.23) * mm});
            skArc(sketch, "E182.trimOffspring", {"start": v(-8.25, 739.2) * mm, "mid": v(-8.64, 739.07) * mm, "end": v(-9.04, 739) * mm});
            skPoint(sketch, "E183.orphan", {"position": v(0.3, 736.11) * mm});
            skArc(sketch, "E184.trimOffspring", {"start": v(-8.25, 739.2) * mm, "mid": v(-7.87, 738.39) * mm, "end": v(-7.37, 737.64) * mm});
            skPoint(sketch, "E185.orphan", {"position": v(-4.77, 746.9) * mm});
            skArc(sketch, "E186.trimOffspring", {"start": v(-36.32, 701.54) * mm, "mid": v(-33.51, 700.95) * mm, "end": v(-30.76, 701.72) * mm});
            skArc(sketch, "E187.trimOffspring", {"start": v(-35.6, 703.17) * mm, "mid": v(-33.6, 702.72) * mm, "end": v(-31.63, 703.27) * mm});
            skArc(sketch, "E188.trimOffspring", {"start": v(-13.1, 703.11) * mm, "mid": v(-15.03, 702.72) * mm, "end": v(-16.93, 703.27) * mm});
            skArc(sketch, "E189.trimOffspring", {"start": v(-12.35, 701.5) * mm, "mid": v(-15.1, 700.95) * mm, "end": v(-17.8, 701.72) * mm});
            skPoint(sketch, "E190.orphan", {"position": v(-39.97, 699.24) * mm});
            skArc(sketch, "E191.trimOffspring", {"start": v(-35.6, 703.17) * mm, "mid": v(-35.88, 702.32) * mm, "end": v(-36.32, 701.54) * mm});
            skPoint(sketch, "E192.orphan", {"position": v(-39.54, 709.66) * mm});
            skPoint(sketch, "E193.orphan", {"position": v(-8.73, 699.24) * mm});
            skArc(sketch, "E194.trimOffspring", {"start": v(-13.1, 703.11) * mm, "mid": v(-12.79, 702.27) * mm, "end": v(-12.35, 701.5) * mm});
            skPoint(sketch, "E195.orphan", {"position": v(-9.15, 709.66) * mm});
            skPoint(sketch, "E196.orphan", {"position": v(-11.98, 710.39) * mm});
            skPoint(sketch, "E197.orphan", {"position": v(-36.58, 710.39) * mm});
            skSolve(sketch);
        }
        {
            var Q0;
            Q0=makeQuery(id+"F3.opExtrude","CAP_FACE",FACE,{"disambiguationData":[OSD([sQuery(id+"F2.wireOp",EDGE,"E1"),sQuery(id+"F2.wireOp",EDGE,"E2"),sQuery(id+"F2.wireOp",EDGE,"E3"),sQuery(id+"F2.wireOp",EDGE,"E8"),sQuery(id+"F2.wireOp",EDGE,"E9"),sQuery(id+"F2.wireOp",EDGE,"E10"),sQuery(id+"F2.wireOp",EDGE,"E11"),sQuery(id+"F2.wireOp",EDGE,"E12.MirrorCS"),sQuery(id+"F2.wireOp",EDGE,"E13.MirrorCS"),sQuery(id+"F2.wireOp",EDGE,"E14.MirrorCS"),sQuery(id+"F2.wireOp",EDGE,"E15.MirrorCS"),sQuery(id+"F2.wireOp",EDGE,"E16.MirrorCS"),sQuery(id+"F2.wireOp",EDGE,"E17.MirrorCS"),sQuery(id+"F2.wireOp",EDGE,"E18.MirrorCS")])],"isStart":false});
            var sketch = newSketch(context, id + "F6", { "sketchPlane" : qUnion([Q0])});
            skArc(sketch, "E198", {"start": v(263.54, 215.43) * mm, "mid": v(6.9, 264.09) * mm, "end": v(-249.74, 215.44) * mm});
            skArc(sketch, "E199", {"start": v(234.25, 142.09) * mm, "mid": v(6.85, 185.62) * mm, "end": v(-220.58, 142.24) * mm});
            skArc(sketch, "E200", {"start": v(200.05, 138.44) * mm, "mid": v(6.82, 169.93) * mm, "end": v(-186.4, 138.37) * mm});
            skArc(sketch, "E201", {"start": v(170.91, 65.18) * mm, "mid": v(6.88, 91.1) * mm, "end": v(-157.16, 65.24) * mm});
            skLineSegment(sketch, "E202", {"start": v(-249.74, 215.44) * mm, "end": v(-220.58, 142.24) * mm});
            skLineSegment(sketch, "E203", {"start": v(-186.4, 138.37) * mm, "end": v(-157.16, 65.24) * mm});
            skLineSegment(sketch, "E204", {"start": v(170.91, 65.18) * mm, "end": v(200.05, 138.44) * mm});
            skLineSegment(sketch, "E205", {"start": v(234.25, 142.09) * mm, "end": v(263.54, 215.43) * mm});
            skSolve(sketch);
        }
        {
            var Q0;
            Q0 = qSketchRegion(id + "F6", true);
            extrude(context, id + "F7", {"entities" : qUnion([Q0]), "operationType" : NewBodyOperationType.ADD, "oppositeDirection" : true, "depth" : 10 * mm, "offsetDistance" : 25.4 * mm});
        }
        {
            var Q0;
            Q0=makeQuery(id+"F7.boolean.opBoolean","MERGE",FACE,{"derivedFrom":[makeQuery(id+"F3.opExtrude","CAP_FACE",FACE,{"disambiguationData":[OSD([sQuery(id+"F2.wireOp",EDGE,"E1"),sQuery(id+"F2.wireOp",EDGE,"E2"),sQuery(id+"F2.wireOp",EDGE,"E3"),sQuery(id+"F2.wireOp",EDGE,"E8"),sQuery(id+"F2.wireOp",EDGE,"E9"),sQuery(id+"F2.wireOp",EDGE,"E10"),sQuery(id+"F2.wireOp",EDGE,"E11"),sQuery(id+"F2.wireOp",EDGE,"E12.MirrorCS"),sQuery(id+"F2.wireOp",EDGE,"E13.MirrorCS"),sQuery(id+"F2.wireOp",EDGE,"E14.MirrorCS"),sQuery(id+"F2.wireOp",EDGE,"E15.MirrorCS"),sQuery(id+"F2.wireOp",EDGE,"E16.MirrorCS"),sQuery(id+"F2.wireOp",EDGE,"E17.MirrorCS"),sQuery(id+"F2.wireOp",EDGE,"E18.MirrorCS")])],"isStart":false}),makeQuery(id+"F7.opExtrude","CAP_FACE",FACE,{"disambiguationData":[OSD([sQuery(id+"F6.wireOp",EDGE,"E198"),sQuery(id+"F6.wireOp",EDGE,"E199"),sQuery(id+"F6.wireOp",EDGE,"E202"),sQuery(id+"F6.wireOp",EDGE,"E205")])],"isStart":true}),makeQuery(id+"F7.opExtrude","CAP_FACE",FACE,{"disambiguationData":[OSD([sQuery(id+"F6.wireOp",EDGE,"E200"),sQuery(id+"F6.wireOp",EDGE,"E201"),sQuery(id+"F6.wireOp",EDGE,"E203"),sQuery(id+"F6.wireOp",EDGE,"E204")])],"isStart":true})]});
            var sketch = newSketch(context, id + "F8", { "sketchPlane" : qUnion([Q0])});
            skArc(sketch, "E206", {"start": v(-180.56, 123.76) * mm, "mid": v(-199.02, 117.23) * mm, "end": v(-217.2, 109.95) * mm});
            skArc(sketch, "E207", {"start": v(-211.43, 95.45) * mm, "mid": v(-233.53, 85.95) * mm, "end": v(-255.06, 75.23) * mm});
            skArc(sketch, "E208", {"start": v(-139.02, 54.62) * mm, "mid": v(-163.8, 46.4) * mm, "end": v(-188.19, 37.07) * mm});
            skArc(sketch, "E209", {"start": v(-162.85, 30.15) * mm, "mid": v(-194.92, 16.98) * mm, "end": v(-226.04, 1.7) * mm});
            skLineSegment(sketch, "E210", {"start": v(-217.2, 109.95) * mm, "end": v(-188.19, 37.07) * mm});
            skLineSegment(sketch, "E211", {"start": v(-226.04, 1.7) * mm, "end": v(-217.2, 45.84) * mm});
            skLineSegment(sketch, "E212", {"start": v(-217.2, 45.84) * mm, "end": v(-255.06, 75.23) * mm});
            skLineSegment(sketch, "E213", {"start": v(-162.85, 30.15) * mm, "end": v(-168.54, 44.69) * mm});
            skLineSegment(sketch, "E214", {"start": v(-139.02, 54.62) * mm, "end": v(-145.34, 74.37) * mm});
            skLineSegment(sketch, "E215", {"start": v(-180.56, 123.76) * mm, "end": v(-145.34, 74.37) * mm});
            skSolve(sketch);
        }
        {
            var Q0;
            Q0 = qSketchRegion(id + "F8", true);
            extrude(context, id + "F9", {"entities" : qUnion([Q0]), "oppositeDirection" : true, "depth" : 10 * mm, "offsetDistance" : 25.4 * mm});
        }
        {
            var Q0;
            Q0=makeQuery(id+"F9.opExtrude","SWEPT_BODY",BODY,{"disambiguationData":[OSD([sQuery(id+"F8.wireOp",EDGE,"E206"),sQuery(id+"F8.wireOp",EDGE,"E207"),sQuery(id+"F8.wireOp",EDGE,"E208"),sQuery(id+"F8.wireOp",EDGE,"E209"),sQuery(id+"F8.wireOp",EDGE,"E210"),sQuery(id+"F8.wireOp",EDGE,"E211"),sQuery(id+"F8.wireOp",EDGE,"E212"),sQuery(id+"F8.wireOp",EDGE,"E213"),sQuery(id+"F8.wireOp",EDGE,"E214"),sQuery(id+"F8.wireOp",EDGE,"E215")])]});
            var Q1;
            Q1=makeQuery(id+"F9.opExtrude","SWEPT_EDGE",EDGE,{"disambiguationData":[OSD([sQuery(id+"F8.wireOp",EDGE,"E208"),sQuery(id+"F8.wireOp",EDGE,"E214")])]});
            transform(context, id + "F10", {"entities" : qUnion([Q0]), "transformType" : TransformType.ROTATION, "transformAxis" : qUnion([Q1]), "angle" : 3 * degree, "makeCopy" : true});
        }
        {
            var Q0;
            Q0=makeQuery(id+"F10.opPattern","COPY",BODY,{"derivedFrom":makeQuery(id+"F9.opExtrude","SWEPT_BODY",BODY,{"disambiguationData":[OSD([sQuery(id+"F8.wireOp",EDGE,"E206"),sQuery(id+"F8.wireOp",EDGE,"E207"),sQuery(id+"F8.wireOp",EDGE,"E208"),sQuery(id+"F8.wireOp",EDGE,"E209"),sQuery(id+"F8.wireOp",EDGE,"E210"),sQuery(id+"F8.wireOp",EDGE,"E211"),sQuery(id+"F8.wireOp",EDGE,"E212"),sQuery(id+"F8.wireOp",EDGE,"E213"),sQuery(id+"F8.wireOp",EDGE,"E214"),sQuery(id+"F8.wireOp",EDGE,"E215")])]}),"instanceName":"1"});
            transform(context, id + "F11", {"entities" : qUnion([Q0]), "transformType" : TransformType.TRANSLATION_3D, "dx" : -59.18 * mm, "dy" : 0 * mm, "dz" : 79.76 * mm, "makeCopy" : false});
        }
        {
            var Q0;
            Q0=sQuery(id+"F2.wireOp",EDGE,"E7");
            cPlane(context, id + "F12", {"entities" : qUnion([Q0]), "cplaneType" : CPlaneType.LINE_ANGLE, "offset" : 25.4 * mm, "angle" : 0 * degree, "width" : 152.4 * mm, "height" : 152.4 * mm});
        }
        {
            var Q0;
            Q0=makeQuery(id+"F9.opExtrude","SWEPT_BODY",BODY,{"disambiguationData":[OSD([sQuery(id+"F8.wireOp",EDGE,"E206"),sQuery(id+"F8.wireOp",EDGE,"E207"),sQuery(id+"F8.wireOp",EDGE,"E208"),sQuery(id+"F8.wireOp",EDGE,"E209"),sQuery(id+"F8.wireOp",EDGE,"E210"),sQuery(id+"F8.wireOp",EDGE,"E211"),sQuery(id+"F8.wireOp",EDGE,"E212"),sQuery(id+"F8.wireOp",EDGE,"E213"),sQuery(id+"F8.wireOp",EDGE,"E214"),sQuery(id+"F8.wireOp",EDGE,"E215")])]});
            var Q1;
            Q1=makeQuery(id+"F10.opPattern","COPY",BODY,{"derivedFrom":makeQuery(id+"F9.opExtrude","SWEPT_BODY",BODY,{"disambiguationData":[OSD([sQuery(id+"F8.wireOp",EDGE,"E206"),sQuery(id+"F8.wireOp",EDGE,"E207"),sQuery(id+"F8.wireOp",EDGE,"E208"),sQuery(id+"F8.wireOp",EDGE,"E209"),sQuery(id+"F8.wireOp",EDGE,"E210"),sQuery(id+"F8.wireOp",EDGE,"E211"),sQuery(id+"F8.wireOp",EDGE,"E212"),sQuery(id+"F8.wireOp",EDGE,"E213"),sQuery(id+"F8.wireOp",EDGE,"E214"),sQuery(id+"F8.wireOp",EDGE,"E215")])]}),"instanceName":"1"});
            var Q2;
            Q2=qCreatedBy(id+"F12.planeOp",FACE);
            mirror(context, id + "F13", {"operationType" : NewBodyOperationType.ADD, "entities" : qUnion([Q0, Q1]), "mirrorPlane" : qUnion([Q2])});
        }
        {
            var Q0;
            Q0=makeQuery(id+"F1.opExtrude","CAP_FACE",FACE,{"disambiguationData":[OSD([sQuery(id+"F0.wireOp",EDGE,"E0")])],"isStart":false});
            var sketch = newSketch(context, id + "F14", { "sketchPlane" : qUnion([Q0])});
            skCircle(sketch, "E216.0", {"center": v(6.77, 469.76) * mm, "radius": 199.91 * mm});
            skLineSegment(sketch, "E217.0.0", {"start": v(-189.02, 690.2) * mm, "end": v(-189.02, 690.2) * mm});
            skLineSegment(sketch, "E217.0.1", {"start": v(-189.02, 427.97) * mm, "end": v(-189.02, 427.97) * mm});
            skLineSegment(sketch, "E217.0.2", {"start": v(-32.56, 121.24) * mm, "end": v(-32.56, 698.67) * mm, "construction": true});
            skArc(sketch, "E217.0.3", {"start": v(-32.56, 698.67) * mm, "mid": v(-110.33, 685.87) * mm, "end": v(-189.02, 690.2) * mm, "construction": true});
            skCircle(sketch, "E218", {"center": v(6.77, 469.76) * mm, "radius": 193.22 * mm});
            skCircle(sketch, "E219", {"center": v(6.77, 469.76) * mm, "radius": 155.81 * mm});
            skCircle(sketch, "E220", {"center": v(6.77, 469.76) * mm, "radius": 148.86 * mm});
            skSolve(sketch);
        }
        {
            var Q0;
            Q0=makeQuery(id+"F14.imprint","IMPRINT",FACE,{"disambiguationData":[TD([[makeQuery(id+"F14.imprint","IMPRINT",EDGE,{"derivedFrom":sQuery(id+"F14.wireOp",EDGE,"E216.0")}),1.0]])]});
            var Q1;
            Q1=makeQuery(id+"F14.imprint","IMPRINT",FACE,{"disambiguationData":[TD([[makeQuery(id+"F14.imprint","IMPRINT",EDGE,{"derivedFrom":sQuery(id+"F14.wireOp",EDGE,"E219")}),1.0]])]});
            extrude(context, id + "F15", {"entities" : qUnion([Q0, Q1]), "operationType" : NewBodyOperationType.REMOVE, "oppositeDirection" : true, "depth" : 0.5 * mm, "offsetDistance" : 25.4 * mm});
        }
        {
            var Q0;
            Q0=makeQuery(id+"F15.boolean.opBoolean","SPLIT",FACE,{"disambiguationData":[TD([makeQuery(id+"F15.opExtrude","SWEPT_FACE",FACE,{"disambiguationData":[OSD([sQuery(id+"F14.wireOp",EDGE,"E220")])]})])],"derivedFrom":makeQuery(id+"F1.opExtrude","CAP_FACE",FACE,{"disambiguationData":[OSD([sQuery(id+"F0.wireOp",EDGE,"E0")])],"isStart":false})});
            var sketch = newSketch(context, id + "F16", { "sketchPlane" : qUnion([Q0])});
            skLineSegment(sketch, "E221", {"start": v(6.77, 469.76) * mm, "end": v(-173.91, 574.08) * mm, "construction": true});
            skLineSegment(sketch, "E222", {"start": v(6.77, 469.76) * mm, "end": v(-139.67, 616.2) * mm, "construction": true});
            skLineSegment(sketch, "E223", {"start": v(6.77, 469.76) * mm, "end": v(-95.9, 647.6) * mm, "construction": true});
            skLineSegment(sketch, "E224", {"start": v(6.77, 469.76) * mm, "end": v(-45.9, 666.35) * mm, "construction": true});
            skLineSegment(sketch, "E225", {"start": v(6.77, 469.76) * mm, "end": v(6.77, 673.22) * mm, "construction": true});
            skLineSegment(sketch, "E226", {"start": v(6.77, 469.76) * mm, "end": v(59.98, 668.37) * mm, "construction": true});
            skLineSegment(sketch, "E227", {"start": v(6.77, 469.76) * mm, "end": v(108.15, 645.37) * mm, "construction": true});
            skLineSegment(sketch, "E228", {"start": v(6.77, 469.76) * mm, "end": v(151.88, 614.88) * mm, "construction": true});
            skLineSegment(sketch, "E229", {"start": v(6.77, 469.76) * mm, "end": v(185.61, 573.02) * mm, "construction": true});
            skCircle(sketch, "E230", {"center": v(6.77, 469.76) * mm, "radius": 157.95 * mm, "construction": true});
            skText(sketch, "E231", { "text": "S", "fontName": "RobotoSlab-Bold.ttf"});
            skCircle(sketch, "E232", {"center": v(6.77, 469.76) * mm, "radius": 191.14 * mm, "construction": true});
            skText(sketch, "E233", { "text": "O", "fontName": "RobotoSlab-Bold.ttf"});
            skText(sketch, "E234", { "text": "U", "fontName": "RobotoSlab-Bold.ttf"});
            skText(sketch, "E235", { "text": "T", "fontName": "RobotoSlab-Bold.ttf"});
            skText(sketch, "E236", { "text": "H", "fontName": "RobotoSlab-Bold.ttf"});
            skText(sketch, "E237", { "text": "O", "fontName": "RobotoSlab-Bold.ttf"});
            skText(sketch, "E238", { "text": "V", "fontName": "RobotoSlab-Bold.ttf"});
            skText(sketch, "E239", { "text": "E", "fontName": "RobotoSlab-Bold.ttf"});
            skText(sketch, "E240", { "text": "R", "fontName": "RobotoSlab-Bold.ttf"});
            const initialGuessF16  = {"E231": [-0.13739, 0.53598, 0.5, 0.86603, 0.0332], "E233": [-0.11696, 0.56942, 0.7071, 0.7071, 0.0332], "E234": [-0.08822, 0.5973, 0.86603, 0.5, 0.0332], "E235": [-0.05002, 0.61807, 0.96593, 0.25882, 0.0332], "E236": [-0.01202, 0.62771, 1, 0, 0.0332], "E237": [0.0312, 0.62674, 0.96593, -0.25882, 0.0332], "E238": [0.07053, 0.61533, 0.86603, -0.5, 0.0332], "E239": [0.10784, 0.59206, 0.7071, -0.7071, 0.0332], "E240": [0.13515, 0.5633, 0.5, -0.86603, 0.0332]};
            skSetInitialGuess(sketch, initialGuessF16);
            skSolve(sketch);
        }
        {
            var Q0;
            Q0 = qSketchRegion(id + "F16", true);
            extrude(context, id + "F17", {"entities" : qUnion([Q0]), "operationType" : NewBodyOperationType.REMOVE, "oppositeDirection" : true, "depth" : 5.08 * mm, "offsetDistance" : 25.4 * mm});
        }
        {
            var Q0;
            Q0=makeQuery(id+"F15.boolean.opBoolean","SPLIT",FACE,{"disambiguationData":[TD([makeQuery(id+"F15.opExtrude","SWEPT_FACE",FACE,{"disambiguationData":[OSD([sQuery(id+"F14.wireOp",EDGE,"E220")])]})])],"derivedFrom":makeQuery(id+"F1.opExtrude","CAP_FACE",FACE,{"disambiguationData":[OSD([sQuery(id+"F0.wireOp",EDGE,"E0")])],"isStart":false})});
            var sketch = newSketch(context, id + "F18", { "sketchPlane" : qUnion([Q0])});
            skLineSegment(sketch, "E241", {"start": v(6.77, 469.76) * mm, "end": v(-47.3, 267.96) * mm, "construction": true});
            skLineSegment(sketch, "E242", {"start": v(6.77, 469.76) * mm, "end": v(-99.13, 286.34) * mm, "construction": true});
            skLineSegment(sketch, "E243", {"start": v(6.77, 469.76) * mm, "end": v(-125.86, 311.7) * mm, "construction": true});
            skLineSegment(sketch, "E244", {"start": v(6.77, 469.76) * mm, "end": v(-151.26, 337.17) * mm, "construction": true});
            skLineSegment(sketch, "E245", {"start": v(6.77, 469.76) * mm, "end": v(-177.6, 383.8) * mm, "construction": true});
            skLineSegment(sketch, "E246", {"start": v(6.77, 469.76) * mm, "end": v(-198.57, 433.56) * mm, "construction": true});
            skLineSegment(sketch, "E247", {"start": v(6.77, 469.76) * mm, "end": v(-209.62, 488.7) * mm, "construction": true});
            skCircle(sketch, "E248", {"center": v(6.77, 469.76) * mm, "radius": 158.5 * mm, "construction": true});
            skCircle(sketch, "E249", {"center": v(6.77, 469.76) * mm, "radius": 190.27 * mm, "construction": true});
            skLineSegment(sketch, "E250.MirrorCS", {"start": v(6.77, 469.76) * mm, "end": v(223.16, 488.7) * mm, "construction": true});
            skLineSegment(sketch, "E251.MirrorCS", {"start": v(6.77, 469.76) * mm, "end": v(212.1, 433.56) * mm, "construction": true});
            skLineSegment(sketch, "E252.MirrorCS", {"start": v(6.77, 469.76) * mm, "end": v(191.13, 383.8) * mm, "construction": true});
            skLineSegment(sketch, "E253.MirrorCS", {"start": v(6.77, 469.76) * mm, "end": v(112.66, 286.34) * mm, "construction": true});
            skLineSegment(sketch, "E254.MirrorCS", {"start": v(6.77, 469.76) * mm, "end": v(60.84, 267.96) * mm, "construction": true});
            skLineSegment(sketch, "E255", {"start": v(6.77, 469.76) * mm, "end": v(158.03, 318.5) * mm, "construction": true});
            skLineSegment(sketch, "E256", {"start": v(6.77, 469.76) * mm, "end": v(184.76, 345.13) * mm, "construction": true});
            skText(sketch, "E257", { "text": "B", "fontName": "RobotoSlab-Bold.ttf"});
            skText(sketch, "E258", { "text": "O", "fontName": "RobotoSlab-Bold.ttf"});
            skText(sketch, "E259", { "text": "N", "fontName": "RobotoSlab-Bold.ttf"});
            skText(sketch, "E260", { "text": "F", "fontName": "RobotoSlab-Bold.ttf"});
            skText(sketch, "E261", { "text": "I", "fontName": "RobotoSlab-Bold.ttf"});
            skText(sketch, "E262", { "text": "R", "fontName": "RobotoSlab-Bold.ttf"});
            skText(sketch, "E263", { "text": "E", "fontName": "RobotoSlab-Bold.ttf"});
            skText(sketch, "E264", { "text": "S", "fontName": "RobotoSlab-Bold.ttf"});
            skText(sketch, "E265", { "text": "O", "fontName": "RobotoSlab-Bold.ttf"});
            skText(sketch, "E266", { "text": "C", "fontName": "RobotoSlab-Bold.ttf"});
            skText(sketch, "E267", { "text": "I", "fontName": "RobotoSlab-Bold.ttf"});
            skText(sketch, "E268", { "text": "E", "fontName": "RobotoSlab-Bold.ttf"});
            skText(sketch, "E269", { "text": "T", "fontName": "RobotoSlab-Bold.ttf"});
            skText(sketch, "E270", { "text": "Y", "fontName": "RobotoSlab-Bold.ttf"});
            const initialGuessF18  = {"E257": [-0.18144, 0.50166, -0.08716, -0.9962, 0.03178], "E258": [-0.18344, 0.45277, 0.17365, -0.9848, 0.03178], "E259": [-0.17328, 0.40565, 0.42262, -0.9063, 0.03178], "E260": [-0.14827, 0.35852, 0.64279, -0.76604, 0.03178], "E261": [-0.122, 0.32943, 0.76604, -0.64279, 0.03178], "E262": [-0.1023, 0.31303, 0.86603, -0.5, 0.03178], "E263": [-0.05636, 0.2897, 0.96593, -0.25882, 0.03178], "E264": [0.0424, 0.28233, 0.96593, 0.25882, 0.03178], "E265": [0.0878, 0.29685, 0.86603, 0.5, 0.03177], "E266": [0.13084, 0.32475, 0.7071, 0.7071, 0.03178], "E267": [0.15779, 0.35371, 0.57358, 0.81915, 0.03178], "E268": [0.17306, 0.37642, 0.42262, 0.9063, 0.03167], "E269": [0.19141, 0.4212, 0.17365, 0.9848, 0.03178], "E270": [0.19729, 0.47009, -0.07424, 0.99724, 0.03154]};
            skSetInitialGuess(sketch, initialGuessF18);
            skSolve(sketch);
        }
        {
            var Q0;
            Q0 = qSketchRegion(id + "F18", true);
            extrude(context, id + "F19", {"entities" : qUnion([Q0]), "operationType" : NewBodyOperationType.REMOVE, "oppositeDirection" : true, "depth" : 5.08 * mm, "offsetDistance" : 25.4 * mm});
        }
        {
            var Q0;
            Q0=makeQuery(id+"F15.boolean.opBoolean","SPLIT",FACE,{"disambiguationData":[TD([makeQuery(id+"F15.opExtrude","SWEPT_FACE",FACE,{"disambiguationData":[OSD([sQuery(id+"F14.wireOp",EDGE,"E220")])]})])],"derivedFrom":makeQuery(id+"F1.opExtrude","CAP_FACE",FACE,{"disambiguationData":[OSD([sQuery(id+"F0.wireOp",EDGE,"E0")])],"isStart":false})});
            var sketch = newSketch(context, id + "F20", { "sketchPlane" : qUnion([Q0])});
            skArc(sketch, "E271", {"start": v(-106.27, 426.16) * mm, "mid": v(-102.04, 438.54) * mm, "end": v(-100.88, 451.57) * mm});
            skArc(sketch, "E272", {"start": v(-106.27, 426.16) * mm, "mid": v(-106.4, 433.18) * mm, "end": v(-109.75, 439.36) * mm});
            skArc(sketch, "E273", {"start": v(-109.75, 439.36) * mm, "mid": v(-109.2, 445.14) * mm, "end": v(-109.03, 450.94) * mm});
            skArc(sketch, "E274", {"start": v(-109.75, 462.3) * mm, "mid": v(-106.52, 464.8) * mm, "end": v(-103.95, 468) * mm});
            skArc(sketch, "E275", {"start": v(-93.78, 459.44) * mm, "mid": v(-97.8, 460.14) * mm, "end": v(-101.88, 460.41) * mm});
            skArc(sketch, "E276", {"start": v(-97.62, 451.05) * mm, "mid": v(-99.24, 451.36) * mm, "end": v(-100.88, 451.57) * mm});
            skArc(sketch, "E277", {"start": v(-97.62, 451.05) * mm, "mid": v(-94.3, 454.6) * mm, "end": v(-93.78, 459.44) * mm});
            skArc(sketch, "E278", {"start": v(-112.6, 459.08) * mm, "mid": v(-116.35, 454.22) * mm, "end": v(-115.82, 448.1) * mm});
            skArc(sketch, "E279", {"start": v(-104.83, 437.13) * mm, "mid": v(-103.22, 445.55) * mm, "end": v(-103.24, 454.12) * mm});
            skArc(sketch, "E280", {"start": v(-106.9, 440.05) * mm, "mid": v(-106.43, 446.94) * mm, "end": v(-106.42, 453.84) * mm});
            skArc(sketch, "E281", {"start": v(-96.24, 457.3) * mm, "mid": v(-100, 457.8) * mm, "end": v(-103.79, 457.92) * mm});
            skArc(sketch, "E282", {"start": v(-97.62, 453.8) * mm, "mid": v(-96.72, 455.46) * mm, "end": v(-96.24, 457.3) * mm});
            skArc(sketch, "E283", {"start": v(-97.62, 453.8) * mm, "mid": v(-100.42, 454.08) * mm, "end": v(-103.24, 454.12) * mm});
            skArc(sketch, "E284", {"start": v(-112, 456.76) * mm, "mid": v(-113.76, 454.54) * mm, "end": v(-114.12, 451.72) * mm});
            skArc(sketch, "E285", {"start": v(-106.9, 461.06) * mm, "mid": v(-105.86, 461.65) * mm, "end": v(-104.83, 462.3) * mm});
            skArc(sketch, "E286", {"start": v(-104.83, 437.13) * mm, "mid": v(-105.74, 438.69) * mm, "end": v(-106.9, 440.05) * mm});
            skArc(sketch, "E287.trimOffspring", {"start": v(-109.47, 459.78) * mm, "mid": v(-109.6, 461.04) * mm, "end": v(-109.75, 462.3) * mm});
            skArc(sketch, "E288.trimOffspring", {"start": v(-109.03, 450.94) * mm, "mid": v(-112.53, 449.78) * mm, "end": v(-115.82, 448.1) * mm});
            skArc(sketch, "E289.trimOffspring", {"start": v(-101.88, 460.41) * mm, "mid": v(-102.78, 464.24) * mm, "end": v(-103.95, 468) * mm});
            skArc(sketch, "E290.trimOffspring", {"start": v(-109.47, 459.78) * mm, "mid": v(-111.04, 459.46) * mm, "end": v(-112.6, 459.08) * mm});
            skArc(sketch, "E291.trimOffspring", {"start": v(-106.62, 457.74) * mm, "mid": v(-106.75, 459.4) * mm, "end": v(-106.9, 461.06) * mm});
            skArc(sketch, "E292.trimOffspring", {"start": v(-106.62, 457.74) * mm, "mid": v(-109.32, 457.35) * mm, "end": v(-112, 456.76) * mm});
            skArc(sketch, "E293.trimOffspring", {"start": v(-106.42, 453.84) * mm, "mid": v(-110.34, 453.03) * mm, "end": v(-114.12, 451.72) * mm});
            skArc(sketch, "E294.trimOffspring", {"start": v(-103.79, 457.92) * mm, "mid": v(-104.25, 460.12) * mm, "end": v(-104.83, 462.3) * mm});
            skSolve(sketch);
        }
        {
            var Q0;
            Q0 = qSketchRegion(id + "F20", true);
            extrude(context, id + "F21", {"entities" : qUnion([Q0]), "oppositeDirection" : true, "depth" : 0.5 * mm, "offsetDistance" : 25.4 * mm});
        }
        {
            var Q0;
            Q0=makeQuery(id+"F21.opExtrude","SWEPT_BODY",BODY,{"disambiguationData":[OSD([sQuery(id+"F20.wireOp",EDGE,"E271"),sQuery(id+"F20.wireOp",EDGE,"E272"),sQuery(id+"F20.wireOp",EDGE,"E273"),sQuery(id+"F20.wireOp",EDGE,"E274"),sQuery(id+"F20.wireOp",EDGE,"E275"),sQuery(id+"F20.wireOp",EDGE,"E276"),sQuery(id+"F20.wireOp",EDGE,"E277"),sQuery(id+"F20.wireOp",EDGE,"E278"),sQuery(id+"F20.wireOp",EDGE,"E279"),sQuery(id+"F20.wireOp",EDGE,"E280"),sQuery(id+"F20.wireOp",EDGE,"E281"),sQuery(id+"F20.wireOp",EDGE,"E282"),sQuery(id+"F20.wireOp",EDGE,"E283"),sQuery(id+"F20.wireOp",EDGE,"E284"),sQuery(id+"F20.wireOp",EDGE,"E285"),sQuery(id+"F20.wireOp",EDGE,"E286"),sQuery(id+"F20.wireOp",EDGE,"E287.trimOffspring"),sQuery(id+"F20.wireOp",EDGE,"E288.trimOffspring"),sQuery(id+"F20.wireOp",EDGE,"E289.trimOffspring"),sQuery(id+"F20.wireOp",EDGE,"E290.trimOffspring"),sQuery(id+"F20.wireOp",EDGE,"E291.trimOffspring"),sQuery(id+"F20.wireOp",EDGE,"E292.trimOffspring"),sQuery(id+"F20.wireOp",EDGE,"E293.trimOffspring"),sQuery(id+"F20.wireOp",EDGE,"E294.trimOffspring")])]});
            transform(context, id + "F22", {"entities" : qUnion([Q0]), "transformType" : TransformType.TRANSLATION_3D, "dx" : -12.95 * mm, "dy" : 0 * mm, "dz" : 33.02 * mm, "makeCopy" : true});
        }
        {
            var Q0;
            Q0=makeQuery(id+"F21.opExtrude","SWEPT_BODY",BODY,{"disambiguationData":[OSD([sQuery(id+"F20.wireOp",EDGE,"E271"),sQuery(id+"F20.wireOp",EDGE,"E272"),sQuery(id+"F20.wireOp",EDGE,"E273"),sQuery(id+"F20.wireOp",EDGE,"E274"),sQuery(id+"F20.wireOp",EDGE,"E275"),sQuery(id+"F20.wireOp",EDGE,"E276"),sQuery(id+"F20.wireOp",EDGE,"E277"),sQuery(id+"F20.wireOp",EDGE,"E278"),sQuery(id+"F20.wireOp",EDGE,"E279"),sQuery(id+"F20.wireOp",EDGE,"E280"),sQuery(id+"F20.wireOp",EDGE,"E281"),sQuery(id+"F20.wireOp",EDGE,"E282"),sQuery(id+"F20.wireOp",EDGE,"E283"),sQuery(id+"F20.wireOp",EDGE,"E284"),sQuery(id+"F20.wireOp",EDGE,"E285"),sQuery(id+"F20.wireOp",EDGE,"E286"),sQuery(id+"F20.wireOp",EDGE,"E287.trimOffspring"),sQuery(id+"F20.wireOp",EDGE,"E288.trimOffspring"),sQuery(id+"F20.wireOp",EDGE,"E289.trimOffspring"),sQuery(id+"F20.wireOp",EDGE,"E290.trimOffspring"),sQuery(id+"F20.wireOp",EDGE,"E291.trimOffspring"),sQuery(id+"F20.wireOp",EDGE,"E292.trimOffspring"),sQuery(id+"F20.wireOp",EDGE,"E293.trimOffspring"),sQuery(id+"F20.wireOp",EDGE,"E294.trimOffspring")])]});
            transform(context, id + "F23", {"entities" : qUnion([Q0]), "transformType" : TransformType.TRANSLATION_3D, "dx" : 24.9 * mm, "dy" : 0 * mm, "dz" : 24.13 * mm, "makeCopy" : true});
        }
        {
            var Q0;
            Q0=makeQuery(id+"F23.opPattern","COPY",BODY,{"derivedFrom":makeQuery(id+"F21.opExtrude","SWEPT_BODY",BODY,{"disambiguationData":[OSD([sQuery(id+"F20.wireOp",EDGE,"E271"),sQuery(id+"F20.wireOp",EDGE,"E272"),sQuery(id+"F20.wireOp",EDGE,"E273"),sQuery(id+"F20.wireOp",EDGE,"E274"),sQuery(id+"F20.wireOp",EDGE,"E275"),sQuery(id+"F20.wireOp",EDGE,"E276"),sQuery(id+"F20.wireOp",EDGE,"E277"),sQuery(id+"F20.wireOp",EDGE,"E278"),sQuery(id+"F20.wireOp",EDGE,"E279"),sQuery(id+"F20.wireOp",EDGE,"E280"),sQuery(id+"F20.wireOp",EDGE,"E281"),sQuery(id+"F20.wireOp",EDGE,"E282"),sQuery(id+"F20.wireOp",EDGE,"E283"),sQuery(id+"F20.wireOp",EDGE,"E284"),sQuery(id+"F20.wireOp",EDGE,"E285"),sQuery(id+"F20.wireOp",EDGE,"E286"),sQuery(id+"F20.wireOp",EDGE,"E287.trimOffspring"),sQuery(id+"F20.wireOp",EDGE,"E288.trimOffspring"),sQuery(id+"F20.wireOp",EDGE,"E289.trimOffspring"),sQuery(id+"F20.wireOp",EDGE,"E290.trimOffspring"),sQuery(id+"F20.wireOp",EDGE,"E291.trimOffspring"),sQuery(id+"F20.wireOp",EDGE,"E292.trimOffspring"),sQuery(id+"F20.wireOp",EDGE,"E293.trimOffspring"),sQuery(id+"F20.wireOp",EDGE,"E294.trimOffspring")])]}),"instanceName":"1"});
            transform(context, id + "F24", {"entities" : qUnion([Q0]), "transformType" : TransformType.TRANSLATION_3D, "dx" : 10.16 * mm, "dy" : 0 * mm, "dz" : 36.58 * mm, "makeCopy" : true});
        }
        {
            var Q0;
            Q0=makeQuery(id+"F24.opPattern","COPY",BODY,{"derivedFrom":makeQuery(id+"F23.opPattern","COPY",BODY,{"derivedFrom":makeQuery(id+"F21.opExtrude","SWEPT_BODY",BODY,{"disambiguationData":[OSD([sQuery(id+"F20.wireOp",EDGE,"E271"),sQuery(id+"F20.wireOp",EDGE,"E272"),sQuery(id+"F20.wireOp",EDGE,"E273"),sQuery(id+"F20.wireOp",EDGE,"E274"),sQuery(id+"F20.wireOp",EDGE,"E275"),sQuery(id+"F20.wireOp",EDGE,"E276"),sQuery(id+"F20.wireOp",EDGE,"E277"),sQuery(id+"F20.wireOp",EDGE,"E278"),sQuery(id+"F20.wireOp",EDGE,"E279"),sQuery(id+"F20.wireOp",EDGE,"E280"),sQuery(id+"F20.wireOp",EDGE,"E281"),sQuery(id+"F20.wireOp",EDGE,"E282"),sQuery(id+"F20.wireOp",EDGE,"E283"),sQuery(id+"F20.wireOp",EDGE,"E284"),sQuery(id+"F20.wireOp",EDGE,"E285"),sQuery(id+"F20.wireOp",EDGE,"E286"),sQuery(id+"F20.wireOp",EDGE,"E287.trimOffspring"),sQuery(id+"F20.wireOp",EDGE,"E288.trimOffspring"),sQuery(id+"F20.wireOp",EDGE,"E289.trimOffspring"),sQuery(id+"F20.wireOp",EDGE,"E290.trimOffspring"),sQuery(id+"F20.wireOp",EDGE,"E291.trimOffspring"),sQuery(id+"F20.wireOp",EDGE,"E292.trimOffspring"),sQuery(id+"F20.wireOp",EDGE,"E293.trimOffspring"),sQuery(id+"F20.wireOp",EDGE,"E294.trimOffspring")])]}),"instanceName":"1"}),"instanceName":"1"});
            transform(context, id + "F25", {"entities" : qUnion([Q0]), "transformType" : TransformType.TRANSLATION_3D, "dx" : -28.96 * mm, "dy" : 0 * mm, "dz" : 11.43 * mm, "makeCopy" : true});
        }
        {
            var Q0;
            Q0=makeQuery(id+"F25.opPattern","COPY",BODY,{"derivedFrom":makeQuery(id+"F24.opPattern","COPY",BODY,{"derivedFrom":makeQuery(id+"F23.opPattern","COPY",BODY,{"derivedFrom":makeQuery(id+"F21.opExtrude","SWEPT_BODY",BODY,{"disambiguationData":[OSD([sQuery(id+"F20.wireOp",EDGE,"E271"),sQuery(id+"F20.wireOp",EDGE,"E272"),sQuery(id+"F20.wireOp",EDGE,"E273"),sQuery(id+"F20.wireOp",EDGE,"E274"),sQuery(id+"F20.wireOp",EDGE,"E275"),sQuery(id+"F20.wireOp",EDGE,"E276"),sQuery(id+"F20.wireOp",EDGE,"E277"),sQuery(id+"F20.wireOp",EDGE,"E278"),sQuery(id+"F20.wireOp",EDGE,"E279"),sQuery(id+"F20.wireOp",EDGE,"E280"),sQuery(id+"F20.wireOp",EDGE,"E281"),sQuery(id+"F20.wireOp",EDGE,"E282"),sQuery(id+"F20.wireOp",EDGE,"E283"),sQuery(id+"F20.wireOp",EDGE,"E284"),sQuery(id+"F20.wireOp",EDGE,"E285"),sQuery(id+"F20.wireOp",EDGE,"E286"),sQuery(id+"F20.wireOp",EDGE,"E287.trimOffspring"),sQuery(id+"F20.wireOp",EDGE,"E288.trimOffspring"),sQuery(id+"F20.wireOp",EDGE,"E289.trimOffspring"),sQuery(id+"F20.wireOp",EDGE,"E290.trimOffspring"),sQuery(id+"F20.wireOp",EDGE,"E291.trimOffspring"),sQuery(id+"F20.wireOp",EDGE,"E292.trimOffspring"),sQuery(id+"F20.wireOp",EDGE,"E293.trimOffspring"),sQuery(id+"F20.wireOp",EDGE,"E294.trimOffspring")])]}),"instanceName":"1"}),"instanceName":"1"}),"instanceName":"1"});
            transform(context, id + "F26", {"entities" : qUnion([Q0]), "transformType" : TransformType.TRANSLATION_3D, "dx" : 15.5 * mm, "dy" : 0 * mm, "dz" : 36.32 * mm, "makeCopy" : true});
        }
        {
            var Q0;
            Q0=makeQuery(id+"F26.opPattern","COPY",BODY,{"derivedFrom":makeQuery(id+"F25.opPattern","COPY",BODY,{"derivedFrom":makeQuery(id+"F24.opPattern","COPY",BODY,{"derivedFrom":makeQuery(id+"F23.opPattern","COPY",BODY,{"derivedFrom":makeQuery(id+"F21.opExtrude","SWEPT_BODY",BODY,{"disambiguationData":[OSD([sQuery(id+"F20.wireOp",EDGE,"E271"),sQuery(id+"F20.wireOp",EDGE,"E272"),sQuery(id+"F20.wireOp",EDGE,"E273"),sQuery(id+"F20.wireOp",EDGE,"E274"),sQuery(id+"F20.wireOp",EDGE,"E275"),sQuery(id+"F20.wireOp",EDGE,"E276"),sQuery(id+"F20.wireOp",EDGE,"E277"),sQuery(id+"F20.wireOp",EDGE,"E278"),sQuery(id+"F20.wireOp",EDGE,"E279"),sQuery(id+"F20.wireOp",EDGE,"E280"),sQuery(id+"F20.wireOp",EDGE,"E281"),sQuery(id+"F20.wireOp",EDGE,"E282"),sQuery(id+"F20.wireOp",EDGE,"E283"),sQuery(id+"F20.wireOp",EDGE,"E284"),sQuery(id+"F20.wireOp",EDGE,"E285"),sQuery(id+"F20.wireOp",EDGE,"E286"),sQuery(id+"F20.wireOp",EDGE,"E287.trimOffspring"),sQuery(id+"F20.wireOp",EDGE,"E288.trimOffspring"),sQuery(id+"F20.wireOp",EDGE,"E289.trimOffspring"),sQuery(id+"F20.wireOp",EDGE,"E290.trimOffspring"),sQuery(id+"F20.wireOp",EDGE,"E291.trimOffspring"),sQuery(id+"F20.wireOp",EDGE,"E292.trimOffspring"),sQuery(id+"F20.wireOp",EDGE,"E293.trimOffspring"),sQuery(id+"F20.wireOp",EDGE,"E294.trimOffspring")])]}),"instanceName":"1"}),"instanceName":"1"}),"instanceName":"1"}),"instanceName":"1"});
            transform(context, id + "F27", {"entities" : qUnion([Q0]), "transformType" : TransformType.TRANSLATION_3D, "dx" : 24.38 * mm, "dy" : 0 * mm, "dz" : -10.4 * mm, "makeCopy" : true});
        }
        {
            var Q0;
            Q0=makeQuery(id+"F27.opPattern","COPY",BODY,{"derivedFrom":makeQuery(id+"F26.opPattern","COPY",BODY,{"derivedFrom":makeQuery(id+"F25.opPattern","COPY",BODY,{"derivedFrom":makeQuery(id+"F24.opPattern","COPY",BODY,{"derivedFrom":makeQuery(id+"F23.opPattern","COPY",BODY,{"derivedFrom":makeQuery(id+"F21.opExtrude","SWEPT_BODY",BODY,{"disambiguationData":[OSD([sQuery(id+"F20.wireOp",EDGE,"E271"),sQuery(id+"F20.wireOp",EDGE,"E272"),sQuery(id+"F20.wireOp",EDGE,"E273"),sQuery(id+"F20.wireOp",EDGE,"E274"),sQuery(id+"F20.wireOp",EDGE,"E275"),sQuery(id+"F20.wireOp",EDGE,"E276"),sQuery(id+"F20.wireOp",EDGE,"E277"),sQuery(id+"F20.wireOp",EDGE,"E278"),sQuery(id+"F20.wireOp",EDGE,"E279"),sQuery(id+"F20.wireOp",EDGE,"E280"),sQuery(id+"F20.wireOp",EDGE,"E281"),sQuery(id+"F20.wireOp",EDGE,"E282"),sQuery(id+"F20.wireOp",EDGE,"E283"),sQuery(id+"F20.wireOp",EDGE,"E284"),sQuery(id+"F20.wireOp",EDGE,"E285"),sQuery(id+"F20.wireOp",EDGE,"E286"),sQuery(id+"F20.wireOp",EDGE,"E287.trimOffspring"),sQuery(id+"F20.wireOp",EDGE,"E288.trimOffspring"),sQuery(id+"F20.wireOp",EDGE,"E289.trimOffspring"),sQuery(id+"F20.wireOp",EDGE,"E290.trimOffspring"),sQuery(id+"F20.wireOp",EDGE,"E291.trimOffspring"),sQuery(id+"F20.wireOp",EDGE,"E292.trimOffspring"),sQuery(id+"F20.wireOp",EDGE,"E293.trimOffspring"),sQuery(id+"F20.wireOp",EDGE,"E294.trimOffspring")])]}),"instanceName":"1"}),"instanceName":"1"}),"instanceName":"1"}),"instanceName":"1"}),"instanceName":"1"});
            transform(context, id + "F28", {"entities" : qUnion([Q0]), "transformType" : TransformType.TRANSLATION_3D, "dx" : 9.4 * mm, "dy" : 0 * mm, "dz" : 35.81 * mm, "makeCopy" : true});
        }
        {
            var Q0;
            Q0=makeQuery(id+"F28.opPattern","COPY",BODY,{"derivedFrom":makeQuery(id+"F27.opPattern","COPY",BODY,{"derivedFrom":makeQuery(id+"F26.opPattern","COPY",BODY,{"derivedFrom":makeQuery(id+"F25.opPattern","COPY",BODY,{"derivedFrom":makeQuery(id+"F24.opPattern","COPY",BODY,{"derivedFrom":makeQuery(id+"F23.opPattern","COPY",BODY,{"derivedFrom":makeQuery(id+"F21.opExtrude","SWEPT_BODY",BODY,{"disambiguationData":[OSD([sQuery(id+"F20.wireOp",EDGE,"E271"),sQuery(id+"F20.wireOp",EDGE,"E272"),sQuery(id+"F20.wireOp",EDGE,"E273"),sQuery(id+"F20.wireOp",EDGE,"E274"),sQuery(id+"F20.wireOp",EDGE,"E275"),sQuery(id+"F20.wireOp",EDGE,"E276"),sQuery(id+"F20.wireOp",EDGE,"E277"),sQuery(id+"F20.wireOp",EDGE,"E278"),sQuery(id+"F20.wireOp",EDGE,"E279"),sQuery(id+"F20.wireOp",EDGE,"E280"),sQuery(id+"F20.wireOp",EDGE,"E281"),sQuery(id+"F20.wireOp",EDGE,"E282"),sQuery(id+"F20.wireOp",EDGE,"E283"),sQuery(id+"F20.wireOp",EDGE,"E284"),sQuery(id+"F20.wireOp",EDGE,"E285"),sQuery(id+"F20.wireOp",EDGE,"E286"),sQuery(id+"F20.wireOp",EDGE,"E287.trimOffspring"),sQuery(id+"F20.wireOp",EDGE,"E288.trimOffspring"),sQuery(id+"F20.wireOp",EDGE,"E289.trimOffspring"),sQuery(id+"F20.wireOp",EDGE,"E290.trimOffspring"),sQuery(id+"F20.wireOp",EDGE,"E291.trimOffspring"),sQuery(id+"F20.wireOp",EDGE,"E292.trimOffspring"),sQuery(id+"F20.wireOp",EDGE,"E293.trimOffspring"),sQuery(id+"F20.wireOp",EDGE,"E294.trimOffspring")])]}),"instanceName":"1"}),"instanceName":"1"}),"instanceName":"1"}),"instanceName":"1"}),"instanceName":"1"}),"instanceName":"1"});
            transform(context, id + "F29", {"entities" : qUnion([Q0]), "transformType" : TransformType.TRANSLATION_3D, "dx" : 79.5 * mm, "dy" : 0 * mm, "dz" : 10.4 * mm, "makeCopy" : true});
        }
        {
            var Q0;
            Q0=makeQuery(id+"F29.opPattern","COPY",BODY,{"derivedFrom":makeQuery(id+"F28.opPattern","COPY",BODY,{"derivedFrom":makeQuery(id+"F27.opPattern","COPY",BODY,{"derivedFrom":makeQuery(id+"F26.opPattern","COPY",BODY,{"derivedFrom":makeQuery(id+"F25.opPattern","COPY",BODY,{"derivedFrom":makeQuery(id+"F24.opPattern","COPY",BODY,{"derivedFrom":makeQuery(id+"F23.opPattern","COPY",BODY,{"derivedFrom":makeQuery(id+"F21.opExtrude","SWEPT_BODY",BODY,{"disambiguationData":[OSD([sQuery(id+"F20.wireOp",EDGE,"E271"),sQuery(id+"F20.wireOp",EDGE,"E272"),sQuery(id+"F20.wireOp",EDGE,"E273"),sQuery(id+"F20.wireOp",EDGE,"E274"),sQuery(id+"F20.wireOp",EDGE,"E275"),sQuery(id+"F20.wireOp",EDGE,"E276"),sQuery(id+"F20.wireOp",EDGE,"E277"),sQuery(id+"F20.wireOp",EDGE,"E278"),sQuery(id+"F20.wireOp",EDGE,"E279"),sQuery(id+"F20.wireOp",EDGE,"E280"),sQuery(id+"F20.wireOp",EDGE,"E281"),sQuery(id+"F20.wireOp",EDGE,"E282"),sQuery(id+"F20.wireOp",EDGE,"E283"),sQuery(id+"F20.wireOp",EDGE,"E284"),sQuery(id+"F20.wireOp",EDGE,"E285"),sQuery(id+"F20.wireOp",EDGE,"E286"),sQuery(id+"F20.wireOp",EDGE,"E287.trimOffspring"),sQuery(id+"F20.wireOp",EDGE,"E288.trimOffspring"),sQuery(id+"F20.wireOp",EDGE,"E289.trimOffspring"),sQuery(id+"F20.wireOp",EDGE,"E290.trimOffspring"),sQuery(id+"F20.wireOp",EDGE,"E291.trimOffspring"),sQuery(id+"F20.wireOp",EDGE,"E292.trimOffspring"),sQuery(id+"F20.wireOp",EDGE,"E293.trimOffspring"),sQuery(id+"F20.wireOp",EDGE,"E294.trimOffspring")])]}),"instanceName":"1"}),"instanceName":"1"}),"instanceName":"1"}),"instanceName":"1"}),"instanceName":"1"}),"instanceName":"1"}),"instanceName":"1"});
            transform(context, id + "F30", {"entities" : qUnion([Q0]), "transformType" : TransformType.TRANSLATION_3D, "dx" : 26.42 * mm, "dy" : 0 * mm, "dz" : -12.95 * mm, "makeCopy" : true});
        }
        {
            var Q0;
            Q0=makeQuery(id+"F30.opPattern","COPY",BODY,{"derivedFrom":makeQuery(id+"F29.opPattern","COPY",BODY,{"derivedFrom":makeQuery(id+"F28.opPattern","COPY",BODY,{"derivedFrom":makeQuery(id+"F27.opPattern","COPY",BODY,{"derivedFrom":makeQuery(id+"F26.opPattern","COPY",BODY,{"derivedFrom":makeQuery(id+"F25.opPattern","COPY",BODY,{"derivedFrom":makeQuery(id+"F24.opPattern","COPY",BODY,{"derivedFrom":makeQuery(id+"F23.opPattern","COPY",BODY,{"derivedFrom":makeQuery(id+"F21.opExtrude","SWEPT_BODY",BODY,{"disambiguationData":[OSD([sQuery(id+"F20.wireOp",EDGE,"E271"),sQuery(id+"F20.wireOp",EDGE,"E272"),sQuery(id+"F20.wireOp",EDGE,"E273"),sQuery(id+"F20.wireOp",EDGE,"E274"),sQuery(id+"F20.wireOp",EDGE,"E275"),sQuery(id+"F20.wireOp",EDGE,"E276"),sQuery(id+"F20.wireOp",EDGE,"E277"),sQuery(id+"F20.wireOp",EDGE,"E278"),sQuery(id+"F20.wireOp",EDGE,"E279"),sQuery(id+"F20.wireOp",EDGE,"E280"),sQuery(id+"F20.wireOp",EDGE,"E281"),sQuery(id+"F20.wireOp",EDGE,"E282"),sQuery(id+"F20.wireOp",EDGE,"E283"),sQuery(id+"F20.wireOp",EDGE,"E284"),sQuery(id+"F20.wireOp",EDGE,"E285"),sQuery(id+"F20.wireOp",EDGE,"E286"),sQuery(id+"F20.wireOp",EDGE,"E287.trimOffspring"),sQuery(id+"F20.wireOp",EDGE,"E288.trimOffspring"),sQuery(id+"F20.wireOp",EDGE,"E289.trimOffspring"),sQuery(id+"F20.wireOp",EDGE,"E290.trimOffspring"),sQuery(id+"F20.wireOp",EDGE,"E291.trimOffspring"),sQuery(id+"F20.wireOp",EDGE,"E292.trimOffspring"),sQuery(id+"F20.wireOp",EDGE,"E293.trimOffspring"),sQuery(id+"F20.wireOp",EDGE,"E294.trimOffspring")])]}),"instanceName":"1"}),"instanceName":"1"}),"instanceName":"1"}),"instanceName":"1"}),"instanceName":"1"}),"instanceName":"1"}),"instanceName":"1"}),"instanceName":"1"});
            transform(context, id + "F31", {"entities" : qUnion([Q0]), "transformType" : TransformType.TRANSLATION_3D, "dx" : 15.75 * mm, "dy" : 0 * mm, "dz" : -32 * mm, "makeCopy" : true});
        }
        {
            var Q0;
            Q0=makeQuery(id+"F31.opPattern","COPY",BODY,{"derivedFrom":makeQuery(id+"F30.opPattern","COPY",BODY,{"derivedFrom":makeQuery(id+"F29.opPattern","COPY",BODY,{"derivedFrom":makeQuery(id+"F28.opPattern","COPY",BODY,{"derivedFrom":makeQuery(id+"F27.opPattern","COPY",BODY,{"derivedFrom":makeQuery(id+"F26.opPattern","COPY",BODY,{"derivedFrom":makeQuery(id+"F25.opPattern","COPY",BODY,{"derivedFrom":makeQuery(id+"F24.opPattern","COPY",BODY,{"derivedFrom":makeQuery(id+"F23.opPattern","COPY",BODY,{"derivedFrom":makeQuery(id+"F21.opExtrude","SWEPT_BODY",BODY,{"disambiguationData":[OSD([sQuery(id+"F20.wireOp",EDGE,"E271"),sQuery(id+"F20.wireOp",EDGE,"E272"),sQuery(id+"F20.wireOp",EDGE,"E273"),sQuery(id+"F20.wireOp",EDGE,"E274"),sQuery(id+"F20.wireOp",EDGE,"E275"),sQuery(id+"F20.wireOp",EDGE,"E276"),sQuery(id+"F20.wireOp",EDGE,"E277"),sQuery(id+"F20.wireOp",EDGE,"E278"),sQuery(id+"F20.wireOp",EDGE,"E279"),sQuery(id+"F20.wireOp",EDGE,"E280"),sQuery(id+"F20.wireOp",EDGE,"E281"),sQuery(id+"F20.wireOp",EDGE,"E282"),sQuery(id+"F20.wireOp",EDGE,"E283"),sQuery(id+"F20.wireOp",EDGE,"E284"),sQuery(id+"F20.wireOp",EDGE,"E285"),sQuery(id+"F20.wireOp",EDGE,"E286"),sQuery(id+"F20.wireOp",EDGE,"E287.trimOffspring"),sQuery(id+"F20.wireOp",EDGE,"E288.trimOffspring"),sQuery(id+"F20.wireOp",EDGE,"E289.trimOffspring"),sQuery(id+"F20.wireOp",EDGE,"E290.trimOffspring"),sQuery(id+"F20.wireOp",EDGE,"E291.trimOffspring"),sQuery(id+"F20.wireOp",EDGE,"E292.trimOffspring"),sQuery(id+"F20.wireOp",EDGE,"E293.trimOffspring"),sQuery(id+"F20.wireOp",EDGE,"E294.trimOffspring")])]}),"instanceName":"1"}),"instanceName":"1"}),"instanceName":"1"}),"instanceName":"1"}),"instanceName":"1"}),"instanceName":"1"}),"instanceName":"1"}),"instanceName":"1"}),"instanceName":"1"});
            transform(context, id + "F32", {"entities" : qUnion([Q0]), "transformType" : TransformType.TRANSLATION_3D, "dx" : 27.18 * mm, "dy" : 0 * mm, "dz" : 10.67 * mm, "makeCopy" : true});
        }
        {
            var Q0;
            Q0=makeQuery(id+"F31.opPattern","COPY",BODY,{"derivedFrom":makeQuery(id+"F30.opPattern","COPY",BODY,{"derivedFrom":makeQuery(id+"F29.opPattern","COPY",BODY,{"derivedFrom":makeQuery(id+"F28.opPattern","COPY",BODY,{"derivedFrom":makeQuery(id+"F27.opPattern","COPY",BODY,{"derivedFrom":makeQuery(id+"F26.opPattern","COPY",BODY,{"derivedFrom":makeQuery(id+"F25.opPattern","COPY",BODY,{"derivedFrom":makeQuery(id+"F24.opPattern","COPY",BODY,{"derivedFrom":makeQuery(id+"F23.opPattern","COPY",BODY,{"derivedFrom":makeQuery(id+"F21.opExtrude","SWEPT_BODY",BODY,{"disambiguationData":[OSD([sQuery(id+"F20.wireOp",EDGE,"E271"),sQuery(id+"F20.wireOp",EDGE,"E272"),sQuery(id+"F20.wireOp",EDGE,"E273"),sQuery(id+"F20.wireOp",EDGE,"E274"),sQuery(id+"F20.wireOp",EDGE,"E275"),sQuery(id+"F20.wireOp",EDGE,"E276"),sQuery(id+"F20.wireOp",EDGE,"E277"),sQuery(id+"F20.wireOp",EDGE,"E278"),sQuery(id+"F20.wireOp",EDGE,"E279"),sQuery(id+"F20.wireOp",EDGE,"E280"),sQuery(id+"F20.wireOp",EDGE,"E281"),sQuery(id+"F20.wireOp",EDGE,"E282"),sQuery(id+"F20.wireOp",EDGE,"E283"),sQuery(id+"F20.wireOp",EDGE,"E284"),sQuery(id+"F20.wireOp",EDGE,"E285"),sQuery(id+"F20.wireOp",EDGE,"E286"),sQuery(id+"F20.wireOp",EDGE,"E287.trimOffspring"),sQuery(id+"F20.wireOp",EDGE,"E288.trimOffspring"),sQuery(id+"F20.wireOp",EDGE,"E289.trimOffspring"),sQuery(id+"F20.wireOp",EDGE,"E290.trimOffspring"),sQuery(id+"F20.wireOp",EDGE,"E291.trimOffspring"),sQuery(id+"F20.wireOp",EDGE,"E292.trimOffspring"),sQuery(id+"F20.wireOp",EDGE,"E293.trimOffspring"),sQuery(id+"F20.wireOp",EDGE,"E294.trimOffspring")])]}),"instanceName":"1"}),"instanceName":"1"}),"instanceName":"1"}),"instanceName":"1"}),"instanceName":"1"}),"instanceName":"1"}),"instanceName":"1"}),"instanceName":"1"}),"instanceName":"1"});
            transform(context, id + "F33", {"entities" : qUnion([Q0]), "transformType" : TransformType.TRANSLATION_3D, "dx" : 13.97 * mm, "dy" : 0 * mm, "dz" : -28.96 * mm, "makeCopy" : true});
        }
        {
            var Q0;
            Q0=makeQuery(id+"F33.opPattern","COPY",BODY,{"derivedFrom":makeQuery(id+"F31.opPattern","COPY",BODY,{"derivedFrom":makeQuery(id+"F30.opPattern","COPY",BODY,{"derivedFrom":makeQuery(id+"F29.opPattern","COPY",BODY,{"derivedFrom":makeQuery(id+"F28.opPattern","COPY",BODY,{"derivedFrom":makeQuery(id+"F27.opPattern","COPY",BODY,{"derivedFrom":makeQuery(id+"F26.opPattern","COPY",BODY,{"derivedFrom":makeQuery(id+"F25.opPattern","COPY",BODY,{"derivedFrom":makeQuery(id+"F24.opPattern","COPY",BODY,{"derivedFrom":makeQuery(id+"F23.opPattern","COPY",BODY,{"derivedFrom":makeQuery(id+"F21.opExtrude","SWEPT_BODY",BODY,{"disambiguationData":[OSD([sQuery(id+"F20.wireOp",EDGE,"E271"),sQuery(id+"F20.wireOp",EDGE,"E272"),sQuery(id+"F20.wireOp",EDGE,"E273"),sQuery(id+"F20.wireOp",EDGE,"E274"),sQuery(id+"F20.wireOp",EDGE,"E275"),sQuery(id+"F20.wireOp",EDGE,"E276"),sQuery(id+"F20.wireOp",EDGE,"E277"),sQuery(id+"F20.wireOp",EDGE,"E278"),sQuery(id+"F20.wireOp",EDGE,"E279"),sQuery(id+"F20.wireOp",EDGE,"E280"),sQuery(id+"F20.wireOp",EDGE,"E281"),sQuery(id+"F20.wireOp",EDGE,"E282"),sQuery(id+"F20.wireOp",EDGE,"E283"),sQuery(id+"F20.wireOp",EDGE,"E284"),sQuery(id+"F20.wireOp",EDGE,"E285"),sQuery(id+"F20.wireOp",EDGE,"E286"),sQuery(id+"F20.wireOp",EDGE,"E287.trimOffspring"),sQuery(id+"F20.wireOp",EDGE,"E288.trimOffspring"),sQuery(id+"F20.wireOp",EDGE,"E289.trimOffspring"),sQuery(id+"F20.wireOp",EDGE,"E290.trimOffspring"),sQuery(id+"F20.wireOp",EDGE,"E291.trimOffspring"),sQuery(id+"F20.wireOp",EDGE,"E292.trimOffspring"),sQuery(id+"F20.wireOp",EDGE,"E293.trimOffspring"),sQuery(id+"F20.wireOp",EDGE,"E294.trimOffspring")])]}),"instanceName":"1"}),"instanceName":"1"}),"instanceName":"1"}),"instanceName":"1"}),"instanceName":"1"}),"instanceName":"1"}),"instanceName":"1"}),"instanceName":"1"}),"instanceName":"1"}),"instanceName":"1"});
            transform(context, id + "F34", {"entities" : qUnion([Q0]), "transformType" : TransformType.TRANSLATION_3D, "dx" : 29.97 * mm, "dy" : 0 * mm, "dz" : 14.73 * mm, "makeCopy" : true});
        }
        {
            var Q0;
            Q0=makeQuery(id+"F33.opPattern","COPY",BODY,{"derivedFrom":makeQuery(id+"F31.opPattern","COPY",BODY,{"derivedFrom":makeQuery(id+"F30.opPattern","COPY",BODY,{"derivedFrom":makeQuery(id+"F29.opPattern","COPY",BODY,{"derivedFrom":makeQuery(id+"F28.opPattern","COPY",BODY,{"derivedFrom":makeQuery(id+"F27.opPattern","COPY",BODY,{"derivedFrom":makeQuery(id+"F26.opPattern","COPY",BODY,{"derivedFrom":makeQuery(id+"F25.opPattern","COPY",BODY,{"derivedFrom":makeQuery(id+"F24.opPattern","COPY",BODY,{"derivedFrom":makeQuery(id+"F23.opPattern","COPY",BODY,{"derivedFrom":makeQuery(id+"F21.opExtrude","SWEPT_BODY",BODY,{"disambiguationData":[OSD([sQuery(id+"F20.wireOp",EDGE,"E271"),sQuery(id+"F20.wireOp",EDGE,"E272"),sQuery(id+"F20.wireOp",EDGE,"E273"),sQuery(id+"F20.wireOp",EDGE,"E274"),sQuery(id+"F20.wireOp",EDGE,"E275"),sQuery(id+"F20.wireOp",EDGE,"E276"),sQuery(id+"F20.wireOp",EDGE,"E277"),sQuery(id+"F20.wireOp",EDGE,"E278"),sQuery(id+"F20.wireOp",EDGE,"E279"),sQuery(id+"F20.wireOp",EDGE,"E280"),sQuery(id+"F20.wireOp",EDGE,"E281"),sQuery(id+"F20.wireOp",EDGE,"E282"),sQuery(id+"F20.wireOp",EDGE,"E283"),sQuery(id+"F20.wireOp",EDGE,"E284"),sQuery(id+"F20.wireOp",EDGE,"E285"),sQuery(id+"F20.wireOp",EDGE,"E286"),sQuery(id+"F20.wireOp",EDGE,"E287.trimOffspring"),sQuery(id+"F20.wireOp",EDGE,"E288.trimOffspring"),sQuery(id+"F20.wireOp",EDGE,"E289.trimOffspring"),sQuery(id+"F20.wireOp",EDGE,"E290.trimOffspring"),sQuery(id+"F20.wireOp",EDGE,"E291.trimOffspring"),sQuery(id+"F20.wireOp",EDGE,"E292.trimOffspring"),sQuery(id+"F20.wireOp",EDGE,"E293.trimOffspring"),sQuery(id+"F20.wireOp",EDGE,"E294.trimOffspring")])]}),"instanceName":"1"}),"instanceName":"1"}),"instanceName":"1"}),"instanceName":"1"}),"instanceName":"1"}),"instanceName":"1"}),"instanceName":"1"}),"instanceName":"1"}),"instanceName":"1"}),"instanceName":"1"});
            transform(context, id + "F35", {"entities" : qUnion([Q0]), "transformType" : TransformType.TRANSLATION_3D, "dx" : 20.07 * mm, "dy" : 0 * mm, "dz" : -37.08 * mm, "makeCopy" : true});
        }
        {
            var Q0;
            Q0=makeQuery(id+"F35.opPattern","COPY",BODY,{"derivedFrom":makeQuery(id+"F33.opPattern","COPY",BODY,{"derivedFrom":makeQuery(id+"F31.opPattern","COPY",BODY,{"derivedFrom":makeQuery(id+"F30.opPattern","COPY",BODY,{"derivedFrom":makeQuery(id+"F29.opPattern","COPY",BODY,{"derivedFrom":makeQuery(id+"F28.opPattern","COPY",BODY,{"derivedFrom":makeQuery(id+"F27.opPattern","COPY",BODY,{"derivedFrom":makeQuery(id+"F26.opPattern","COPY",BODY,{"derivedFrom":makeQuery(id+"F25.opPattern","COPY",BODY,{"derivedFrom":makeQuery(id+"F24.opPattern","COPY",BODY,{"derivedFrom":makeQuery(id+"F23.opPattern","COPY",BODY,{"derivedFrom":makeQuery(id+"F21.opExtrude","SWEPT_BODY",BODY,{"disambiguationData":[OSD([sQuery(id+"F20.wireOp",EDGE,"E271"),sQuery(id+"F20.wireOp",EDGE,"E272"),sQuery(id+"F20.wireOp",EDGE,"E273"),sQuery(id+"F20.wireOp",EDGE,"E274"),sQuery(id+"F20.wireOp",EDGE,"E275"),sQuery(id+"F20.wireOp",EDGE,"E276"),sQuery(id+"F20.wireOp",EDGE,"E277"),sQuery(id+"F20.wireOp",EDGE,"E278"),sQuery(id+"F20.wireOp",EDGE,"E279"),sQuery(id+"F20.wireOp",EDGE,"E280"),sQuery(id+"F20.wireOp",EDGE,"E281"),sQuery(id+"F20.wireOp",EDGE,"E282"),sQuery(id+"F20.wireOp",EDGE,"E283"),sQuery(id+"F20.wireOp",EDGE,"E284"),sQuery(id+"F20.wireOp",EDGE,"E285"),sQuery(id+"F20.wireOp",EDGE,"E286"),sQuery(id+"F20.wireOp",EDGE,"E287.trimOffspring"),sQuery(id+"F20.wireOp",EDGE,"E288.trimOffspring"),sQuery(id+"F20.wireOp",EDGE,"E289.trimOffspring"),sQuery(id+"F20.wireOp",EDGE,"E290.trimOffspring"),sQuery(id+"F20.wireOp",EDGE,"E291.trimOffspring"),sQuery(id+"F20.wireOp",EDGE,"E292.trimOffspring"),sQuery(id+"F20.wireOp",EDGE,"E293.trimOffspring"),sQuery(id+"F20.wireOp",EDGE,"E294.trimOffspring")])]}),"instanceName":"1"}),"instanceName":"1"}),"instanceName":"1"}),"instanceName":"1"}),"instanceName":"1"}),"instanceName":"1"}),"instanceName":"1"}),"instanceName":"1"}),"instanceName":"1"}),"instanceName":"1"}),"instanceName":"1"});
            transform(context, id + "F36", {"entities" : qUnion([Q0]), "transformType" : TransformType.TRANSLATION_3D, "dx" : 24.64 * mm, "dy" : 0 * mm, "dz" : 19.56 * mm, "makeCopy" : true});
        }
        {
            var Q0;
            Q0=makeQuery(id+"F35.opPattern","COPY",BODY,{"derivedFrom":makeQuery(id+"F33.opPattern","COPY",BODY,{"derivedFrom":makeQuery(id+"F31.opPattern","COPY",BODY,{"derivedFrom":makeQuery(id+"F30.opPattern","COPY",BODY,{"derivedFrom":makeQuery(id+"F29.opPattern","COPY",BODY,{"derivedFrom":makeQuery(id+"F28.opPattern","COPY",BODY,{"derivedFrom":makeQuery(id+"F27.opPattern","COPY",BODY,{"derivedFrom":makeQuery(id+"F26.opPattern","COPY",BODY,{"derivedFrom":makeQuery(id+"F25.opPattern","COPY",BODY,{"derivedFrom":makeQuery(id+"F24.opPattern","COPY",BODY,{"derivedFrom":makeQuery(id+"F23.opPattern","COPY",BODY,{"derivedFrom":makeQuery(id+"F21.opExtrude","SWEPT_BODY",BODY,{"disambiguationData":[OSD([sQuery(id+"F20.wireOp",EDGE,"E271"),sQuery(id+"F20.wireOp",EDGE,"E272"),sQuery(id+"F20.wireOp",EDGE,"E273"),sQuery(id+"F20.wireOp",EDGE,"E274"),sQuery(id+"F20.wireOp",EDGE,"E275"),sQuery(id+"F20.wireOp",EDGE,"E276"),sQuery(id+"F20.wireOp",EDGE,"E277"),sQuery(id+"F20.wireOp",EDGE,"E278"),sQuery(id+"F20.wireOp",EDGE,"E279"),sQuery(id+"F20.wireOp",EDGE,"E280"),sQuery(id+"F20.wireOp",EDGE,"E281"),sQuery(id+"F20.wireOp",EDGE,"E282"),sQuery(id+"F20.wireOp",EDGE,"E283"),sQuery(id+"F20.wireOp",EDGE,"E284"),sQuery(id+"F20.wireOp",EDGE,"E285"),sQuery(id+"F20.wireOp",EDGE,"E286"),sQuery(id+"F20.wireOp",EDGE,"E287.trimOffspring"),sQuery(id+"F20.wireOp",EDGE,"E288.trimOffspring"),sQuery(id+"F20.wireOp",EDGE,"E289.trimOffspring"),sQuery(id+"F20.wireOp",EDGE,"E290.trimOffspring"),sQuery(id+"F20.wireOp",EDGE,"E291.trimOffspring"),sQuery(id+"F20.wireOp",EDGE,"E292.trimOffspring"),sQuery(id+"F20.wireOp",EDGE,"E293.trimOffspring"),sQuery(id+"F20.wireOp",EDGE,"E294.trimOffspring")])]}),"instanceName":"1"}),"instanceName":"1"}),"instanceName":"1"}),"instanceName":"1"}),"instanceName":"1"}),"instanceName":"1"}),"instanceName":"1"}),"instanceName":"1"}),"instanceName":"1"}),"instanceName":"1"}),"instanceName":"1"});
            transform(context, id + "F37", {"entities" : qUnion([Q0]), "transformType" : TransformType.TRANSLATION_3D, "dx" : 27.43 * mm, "dy" : 0 * mm, "dz" : -29.72 * mm, "makeCopy" : true});
        }
        {
            var Q0;
            Q0=makeQuery(id+"F37.opPattern","COPY",BODY,{"derivedFrom":makeQuery(id+"F35.opPattern","COPY",BODY,{"derivedFrom":makeQuery(id+"F33.opPattern","COPY",BODY,{"derivedFrom":makeQuery(id+"F31.opPattern","COPY",BODY,{"derivedFrom":makeQuery(id+"F30.opPattern","COPY",BODY,{"derivedFrom":makeQuery(id+"F29.opPattern","COPY",BODY,{"derivedFrom":makeQuery(id+"F28.opPattern","COPY",BODY,{"derivedFrom":makeQuery(id+"F27.opPattern","COPY",BODY,{"derivedFrom":makeQuery(id+"F26.opPattern","COPY",BODY,{"derivedFrom":makeQuery(id+"F25.opPattern","COPY",BODY,{"derivedFrom":makeQuery(id+"F24.opPattern","COPY",BODY,{"derivedFrom":makeQuery(id+"F23.opPattern","COPY",BODY,{"derivedFrom":makeQuery(id+"F21.opExtrude","SWEPT_BODY",BODY,{"disambiguationData":[OSD([sQuery(id+"F20.wireOp",EDGE,"E271"),sQuery(id+"F20.wireOp",EDGE,"E272"),sQuery(id+"F20.wireOp",EDGE,"E273"),sQuery(id+"F20.wireOp",EDGE,"E274"),sQuery(id+"F20.wireOp",EDGE,"E275"),sQuery(id+"F20.wireOp",EDGE,"E276"),sQuery(id+"F20.wireOp",EDGE,"E277"),sQuery(id+"F20.wireOp",EDGE,"E278"),sQuery(id+"F20.wireOp",EDGE,"E279"),sQuery(id+"F20.wireOp",EDGE,"E280"),sQuery(id+"F20.wireOp",EDGE,"E281"),sQuery(id+"F20.wireOp",EDGE,"E282"),sQuery(id+"F20.wireOp",EDGE,"E283"),sQuery(id+"F20.wireOp",EDGE,"E284"),sQuery(id+"F20.wireOp",EDGE,"E285"),sQuery(id+"F20.wireOp",EDGE,"E286"),sQuery(id+"F20.wireOp",EDGE,"E287.trimOffspring"),sQuery(id+"F20.wireOp",EDGE,"E288.trimOffspring"),sQuery(id+"F20.wireOp",EDGE,"E289.trimOffspring"),sQuery(id+"F20.wireOp",EDGE,"E290.trimOffspring"),sQuery(id+"F20.wireOp",EDGE,"E291.trimOffspring"),sQuery(id+"F20.wireOp",EDGE,"E292.trimOffspring"),sQuery(id+"F20.wireOp",EDGE,"E293.trimOffspring"),sQuery(id+"F20.wireOp",EDGE,"E294.trimOffspring")])]}),"instanceName":"1"}),"instanceName":"1"}),"instanceName":"1"}),"instanceName":"1"}),"instanceName":"1"}),"instanceName":"1"}),"instanceName":"1"}),"instanceName":"1"}),"instanceName":"1"}),"instanceName":"1"}),"instanceName":"1"}),"instanceName":"1"});
            var Q1;
            Q1=makeQuery(id+"F36.opPattern","COPY",BODY,{"derivedFrom":makeQuery(id+"F35.opPattern","COPY",BODY,{"derivedFrom":makeQuery(id+"F33.opPattern","COPY",BODY,{"derivedFrom":makeQuery(id+"F31.opPattern","COPY",BODY,{"derivedFrom":makeQuery(id+"F30.opPattern","COPY",BODY,{"derivedFrom":makeQuery(id+"F29.opPattern","COPY",BODY,{"derivedFrom":makeQuery(id+"F28.opPattern","COPY",BODY,{"derivedFrom":makeQuery(id+"F27.opPattern","COPY",BODY,{"derivedFrom":makeQuery(id+"F26.opPattern","COPY",BODY,{"derivedFrom":makeQuery(id+"F25.opPattern","COPY",BODY,{"derivedFrom":makeQuery(id+"F24.opPattern","COPY",BODY,{"derivedFrom":makeQuery(id+"F23.opPattern","COPY",BODY,{"derivedFrom":makeQuery(id+"F21.opExtrude","SWEPT_BODY",BODY,{"disambiguationData":[OSD([sQuery(id+"F20.wireOp",EDGE,"E271"),sQuery(id+"F20.wireOp",EDGE,"E272"),sQuery(id+"F20.wireOp",EDGE,"E273"),sQuery(id+"F20.wireOp",EDGE,"E274"),sQuery(id+"F20.wireOp",EDGE,"E275"),sQuery(id+"F20.wireOp",EDGE,"E276"),sQuery(id+"F20.wireOp",EDGE,"E277"),sQuery(id+"F20.wireOp",EDGE,"E278"),sQuery(id+"F20.wireOp",EDGE,"E279"),sQuery(id+"F20.wireOp",EDGE,"E280"),sQuery(id+"F20.wireOp",EDGE,"E281"),sQuery(id+"F20.wireOp",EDGE,"E282"),sQuery(id+"F20.wireOp",EDGE,"E283"),sQuery(id+"F20.wireOp",EDGE,"E284"),sQuery(id+"F20.wireOp",EDGE,"E285"),sQuery(id+"F20.wireOp",EDGE,"E286"),sQuery(id+"F20.wireOp",EDGE,"E287.trimOffspring"),sQuery(id+"F20.wireOp",EDGE,"E288.trimOffspring"),sQuery(id+"F20.wireOp",EDGE,"E289.trimOffspring"),sQuery(id+"F20.wireOp",EDGE,"E290.trimOffspring"),sQuery(id+"F20.wireOp",EDGE,"E291.trimOffspring"),sQuery(id+"F20.wireOp",EDGE,"E292.trimOffspring"),sQuery(id+"F20.wireOp",EDGE,"E293.trimOffspring"),sQuery(id+"F20.wireOp",EDGE,"E294.trimOffspring")])]}),"instanceName":"1"}),"instanceName":"1"}),"instanceName":"1"}),"instanceName":"1"}),"instanceName":"1"}),"instanceName":"1"}),"instanceName":"1"}),"instanceName":"1"}),"instanceName":"1"}),"instanceName":"1"}),"instanceName":"1"}),"instanceName":"1"});
            var Q2;
            Q2=makeQuery(id+"F35.opPattern","COPY",BODY,{"derivedFrom":makeQuery(id+"F33.opPattern","COPY",BODY,{"derivedFrom":makeQuery(id+"F31.opPattern","COPY",BODY,{"derivedFrom":makeQuery(id+"F30.opPattern","COPY",BODY,{"derivedFrom":makeQuery(id+"F29.opPattern","COPY",BODY,{"derivedFrom":makeQuery(id+"F28.opPattern","COPY",BODY,{"derivedFrom":makeQuery(id+"F27.opPattern","COPY",BODY,{"derivedFrom":makeQuery(id+"F26.opPattern","COPY",BODY,{"derivedFrom":makeQuery(id+"F25.opPattern","COPY",BODY,{"derivedFrom":makeQuery(id+"F24.opPattern","COPY",BODY,{"derivedFrom":makeQuery(id+"F23.opPattern","COPY",BODY,{"derivedFrom":makeQuery(id+"F21.opExtrude","SWEPT_BODY",BODY,{"disambiguationData":[OSD([sQuery(id+"F20.wireOp",EDGE,"E271"),sQuery(id+"F20.wireOp",EDGE,"E272"),sQuery(id+"F20.wireOp",EDGE,"E273"),sQuery(id+"F20.wireOp",EDGE,"E274"),sQuery(id+"F20.wireOp",EDGE,"E275"),sQuery(id+"F20.wireOp",EDGE,"E276"),sQuery(id+"F20.wireOp",EDGE,"E277"),sQuery(id+"F20.wireOp",EDGE,"E278"),sQuery(id+"F20.wireOp",EDGE,"E279"),sQuery(id+"F20.wireOp",EDGE,"E280"),sQuery(id+"F20.wireOp",EDGE,"E281"),sQuery(id+"F20.wireOp",EDGE,"E282"),sQuery(id+"F20.wireOp",EDGE,"E283"),sQuery(id+"F20.wireOp",EDGE,"E284"),sQuery(id+"F20.wireOp",EDGE,"E285"),sQuery(id+"F20.wireOp",EDGE,"E286"),sQuery(id+"F20.wireOp",EDGE,"E287.trimOffspring"),sQuery(id+"F20.wireOp",EDGE,"E288.trimOffspring"),sQuery(id+"F20.wireOp",EDGE,"E289.trimOffspring"),sQuery(id+"F20.wireOp",EDGE,"E290.trimOffspring"),sQuery(id+"F20.wireOp",EDGE,"E291.trimOffspring"),sQuery(id+"F20.wireOp",EDGE,"E292.trimOffspring"),sQuery(id+"F20.wireOp",EDGE,"E293.trimOffspring"),sQuery(id+"F20.wireOp",EDGE,"E294.trimOffspring")])]}),"instanceName":"1"}),"instanceName":"1"}),"instanceName":"1"}),"instanceName":"1"}),"instanceName":"1"}),"instanceName":"1"}),"instanceName":"1"}),"instanceName":"1"}),"instanceName":"1"}),"instanceName":"1"}),"instanceName":"1"});
            var Q3;
            Q3=makeQuery(id+"F34.opPattern","COPY",BODY,{"derivedFrom":makeQuery(id+"F33.opPattern","COPY",BODY,{"derivedFrom":makeQuery(id+"F31.opPattern","COPY",BODY,{"derivedFrom":makeQuery(id+"F30.opPattern","COPY",BODY,{"derivedFrom":makeQuery(id+"F29.opPattern","COPY",BODY,{"derivedFrom":makeQuery(id+"F28.opPattern","COPY",BODY,{"derivedFrom":makeQuery(id+"F27.opPattern","COPY",BODY,{"derivedFrom":makeQuery(id+"F26.opPattern","COPY",BODY,{"derivedFrom":makeQuery(id+"F25.opPattern","COPY",BODY,{"derivedFrom":makeQuery(id+"F24.opPattern","COPY",BODY,{"derivedFrom":makeQuery(id+"F23.opPattern","COPY",BODY,{"derivedFrom":makeQuery(id+"F21.opExtrude","SWEPT_BODY",BODY,{"disambiguationData":[OSD([sQuery(id+"F20.wireOp",EDGE,"E271"),sQuery(id+"F20.wireOp",EDGE,"E272"),sQuery(id+"F20.wireOp",EDGE,"E273"),sQuery(id+"F20.wireOp",EDGE,"E274"),sQuery(id+"F20.wireOp",EDGE,"E275"),sQuery(id+"F20.wireOp",EDGE,"E276"),sQuery(id+"F20.wireOp",EDGE,"E277"),sQuery(id+"F20.wireOp",EDGE,"E278"),sQuery(id+"F20.wireOp",EDGE,"E279"),sQuery(id+"F20.wireOp",EDGE,"E280"),sQuery(id+"F20.wireOp",EDGE,"E281"),sQuery(id+"F20.wireOp",EDGE,"E282"),sQuery(id+"F20.wireOp",EDGE,"E283"),sQuery(id+"F20.wireOp",EDGE,"E284"),sQuery(id+"F20.wireOp",EDGE,"E285"),sQuery(id+"F20.wireOp",EDGE,"E286"),sQuery(id+"F20.wireOp",EDGE,"E287.trimOffspring"),sQuery(id+"F20.wireOp",EDGE,"E288.trimOffspring"),sQuery(id+"F20.wireOp",EDGE,"E289.trimOffspring"),sQuery(id+"F20.wireOp",EDGE,"E290.trimOffspring"),sQuery(id+"F20.wireOp",EDGE,"E291.trimOffspring"),sQuery(id+"F20.wireOp",EDGE,"E292.trimOffspring"),sQuery(id+"F20.wireOp",EDGE,"E293.trimOffspring"),sQuery(id+"F20.wireOp",EDGE,"E294.trimOffspring")])]}),"instanceName":"1"}),"instanceName":"1"}),"instanceName":"1"}),"instanceName":"1"}),"instanceName":"1"}),"instanceName":"1"}),"instanceName":"1"}),"instanceName":"1"}),"instanceName":"1"}),"instanceName":"1"}),"instanceName":"1"});
            var Q4;
            Q4=makeQuery(id+"F33.opPattern","COPY",BODY,{"derivedFrom":makeQuery(id+"F31.opPattern","COPY",BODY,{"derivedFrom":makeQuery(id+"F30.opPattern","COPY",BODY,{"derivedFrom":makeQuery(id+"F29.opPattern","COPY",BODY,{"derivedFrom":makeQuery(id+"F28.opPattern","COPY",BODY,{"derivedFrom":makeQuery(id+"F27.opPattern","COPY",BODY,{"derivedFrom":makeQuery(id+"F26.opPattern","COPY",BODY,{"derivedFrom":makeQuery(id+"F25.opPattern","COPY",BODY,{"derivedFrom":makeQuery(id+"F24.opPattern","COPY",BODY,{"derivedFrom":makeQuery(id+"F23.opPattern","COPY",BODY,{"derivedFrom":makeQuery(id+"F21.opExtrude","SWEPT_BODY",BODY,{"disambiguationData":[OSD([sQuery(id+"F20.wireOp",EDGE,"E271"),sQuery(id+"F20.wireOp",EDGE,"E272"),sQuery(id+"F20.wireOp",EDGE,"E273"),sQuery(id+"F20.wireOp",EDGE,"E274"),sQuery(id+"F20.wireOp",EDGE,"E275"),sQuery(id+"F20.wireOp",EDGE,"E276"),sQuery(id+"F20.wireOp",EDGE,"E277"),sQuery(id+"F20.wireOp",EDGE,"E278"),sQuery(id+"F20.wireOp",EDGE,"E279"),sQuery(id+"F20.wireOp",EDGE,"E280"),sQuery(id+"F20.wireOp",EDGE,"E281"),sQuery(id+"F20.wireOp",EDGE,"E282"),sQuery(id+"F20.wireOp",EDGE,"E283"),sQuery(id+"F20.wireOp",EDGE,"E284"),sQuery(id+"F20.wireOp",EDGE,"E285"),sQuery(id+"F20.wireOp",EDGE,"E286"),sQuery(id+"F20.wireOp",EDGE,"E287.trimOffspring"),sQuery(id+"F20.wireOp",EDGE,"E288.trimOffspring"),sQuery(id+"F20.wireOp",EDGE,"E289.trimOffspring"),sQuery(id+"F20.wireOp",EDGE,"E290.trimOffspring"),sQuery(id+"F20.wireOp",EDGE,"E291.trimOffspring"),sQuery(id+"F20.wireOp",EDGE,"E292.trimOffspring"),sQuery(id+"F20.wireOp",EDGE,"E293.trimOffspring"),sQuery(id+"F20.wireOp",EDGE,"E294.trimOffspring")])]}),"instanceName":"1"}),"instanceName":"1"}),"instanceName":"1"}),"instanceName":"1"}),"instanceName":"1"}),"instanceName":"1"}),"instanceName":"1"}),"instanceName":"1"}),"instanceName":"1"}),"instanceName":"1"});
            var Q5;
            Q5=makeQuery(id+"F32.opPattern","COPY",BODY,{"derivedFrom":makeQuery(id+"F31.opPattern","COPY",BODY,{"derivedFrom":makeQuery(id+"F30.opPattern","COPY",BODY,{"derivedFrom":makeQuery(id+"F29.opPattern","COPY",BODY,{"derivedFrom":makeQuery(id+"F28.opPattern","COPY",BODY,{"derivedFrom":makeQuery(id+"F27.opPattern","COPY",BODY,{"derivedFrom":makeQuery(id+"F26.opPattern","COPY",BODY,{"derivedFrom":makeQuery(id+"F25.opPattern","COPY",BODY,{"derivedFrom":makeQuery(id+"F24.opPattern","COPY",BODY,{"derivedFrom":makeQuery(id+"F23.opPattern","COPY",BODY,{"derivedFrom":makeQuery(id+"F21.opExtrude","SWEPT_BODY",BODY,{"disambiguationData":[OSD([sQuery(id+"F20.wireOp",EDGE,"E271"),sQuery(id+"F20.wireOp",EDGE,"E272"),sQuery(id+"F20.wireOp",EDGE,"E273"),sQuery(id+"F20.wireOp",EDGE,"E274"),sQuery(id+"F20.wireOp",EDGE,"E275"),sQuery(id+"F20.wireOp",EDGE,"E276"),sQuery(id+"F20.wireOp",EDGE,"E277"),sQuery(id+"F20.wireOp",EDGE,"E278"),sQuery(id+"F20.wireOp",EDGE,"E279"),sQuery(id+"F20.wireOp",EDGE,"E280"),sQuery(id+"F20.wireOp",EDGE,"E281"),sQuery(id+"F20.wireOp",EDGE,"E282"),sQuery(id+"F20.wireOp",EDGE,"E283"),sQuery(id+"F20.wireOp",EDGE,"E284"),sQuery(id+"F20.wireOp",EDGE,"E285"),sQuery(id+"F20.wireOp",EDGE,"E286"),sQuery(id+"F20.wireOp",EDGE,"E287.trimOffspring"),sQuery(id+"F20.wireOp",EDGE,"E288.trimOffspring"),sQuery(id+"F20.wireOp",EDGE,"E289.trimOffspring"),sQuery(id+"F20.wireOp",EDGE,"E290.trimOffspring"),sQuery(id+"F20.wireOp",EDGE,"E291.trimOffspring"),sQuery(id+"F20.wireOp",EDGE,"E292.trimOffspring"),sQuery(id+"F20.wireOp",EDGE,"E293.trimOffspring"),sQuery(id+"F20.wireOp",EDGE,"E294.trimOffspring")])]}),"instanceName":"1"}),"instanceName":"1"}),"instanceName":"1"}),"instanceName":"1"}),"instanceName":"1"}),"instanceName":"1"}),"instanceName":"1"}),"instanceName":"1"}),"instanceName":"1"}),"instanceName":"1"});
            var Q6;
            Q6=makeQuery(id+"F31.opPattern","COPY",BODY,{"derivedFrom":makeQuery(id+"F30.opPattern","COPY",BODY,{"derivedFrom":makeQuery(id+"F29.opPattern","COPY",BODY,{"derivedFrom":makeQuery(id+"F28.opPattern","COPY",BODY,{"derivedFrom":makeQuery(id+"F27.opPattern","COPY",BODY,{"derivedFrom":makeQuery(id+"F26.opPattern","COPY",BODY,{"derivedFrom":makeQuery(id+"F25.opPattern","COPY",BODY,{"derivedFrom":makeQuery(id+"F24.opPattern","COPY",BODY,{"derivedFrom":makeQuery(id+"F23.opPattern","COPY",BODY,{"derivedFrom":makeQuery(id+"F21.opExtrude","SWEPT_BODY",BODY,{"disambiguationData":[OSD([sQuery(id+"F20.wireOp",EDGE,"E271"),sQuery(id+"F20.wireOp",EDGE,"E272"),sQuery(id+"F20.wireOp",EDGE,"E273"),sQuery(id+"F20.wireOp",EDGE,"E274"),sQuery(id+"F20.wireOp",EDGE,"E275"),sQuery(id+"F20.wireOp",EDGE,"E276"),sQuery(id+"F20.wireOp",EDGE,"E277"),sQuery(id+"F20.wireOp",EDGE,"E278"),sQuery(id+"F20.wireOp",EDGE,"E279"),sQuery(id+"F20.wireOp",EDGE,"E280"),sQuery(id+"F20.wireOp",EDGE,"E281"),sQuery(id+"F20.wireOp",EDGE,"E282"),sQuery(id+"F20.wireOp",EDGE,"E283"),sQuery(id+"F20.wireOp",EDGE,"E284"),sQuery(id+"F20.wireOp",EDGE,"E285"),sQuery(id+"F20.wireOp",EDGE,"E286"),sQuery(id+"F20.wireOp",EDGE,"E287.trimOffspring"),sQuery(id+"F20.wireOp",EDGE,"E288.trimOffspring"),sQuery(id+"F20.wireOp",EDGE,"E289.trimOffspring"),sQuery(id+"F20.wireOp",EDGE,"E290.trimOffspring"),sQuery(id+"F20.wireOp",EDGE,"E291.trimOffspring"),sQuery(id+"F20.wireOp",EDGE,"E292.trimOffspring"),sQuery(id+"F20.wireOp",EDGE,"E293.trimOffspring"),sQuery(id+"F20.wireOp",EDGE,"E294.trimOffspring")])]}),"instanceName":"1"}),"instanceName":"1"}),"instanceName":"1"}),"instanceName":"1"}),"instanceName":"1"}),"instanceName":"1"}),"instanceName":"1"}),"instanceName":"1"}),"instanceName":"1"});
            var Q7;
            Q7=makeQuery(id+"F30.opPattern","COPY",BODY,{"derivedFrom":makeQuery(id+"F29.opPattern","COPY",BODY,{"derivedFrom":makeQuery(id+"F28.opPattern","COPY",BODY,{"derivedFrom":makeQuery(id+"F27.opPattern","COPY",BODY,{"derivedFrom":makeQuery(id+"F26.opPattern","COPY",BODY,{"derivedFrom":makeQuery(id+"F25.opPattern","COPY",BODY,{"derivedFrom":makeQuery(id+"F24.opPattern","COPY",BODY,{"derivedFrom":makeQuery(id+"F23.opPattern","COPY",BODY,{"derivedFrom":makeQuery(id+"F21.opExtrude","SWEPT_BODY",BODY,{"disambiguationData":[OSD([sQuery(id+"F20.wireOp",EDGE,"E271"),sQuery(id+"F20.wireOp",EDGE,"E272"),sQuery(id+"F20.wireOp",EDGE,"E273"),sQuery(id+"F20.wireOp",EDGE,"E274"),sQuery(id+"F20.wireOp",EDGE,"E275"),sQuery(id+"F20.wireOp",EDGE,"E276"),sQuery(id+"F20.wireOp",EDGE,"E277"),sQuery(id+"F20.wireOp",EDGE,"E278"),sQuery(id+"F20.wireOp",EDGE,"E279"),sQuery(id+"F20.wireOp",EDGE,"E280"),sQuery(id+"F20.wireOp",EDGE,"E281"),sQuery(id+"F20.wireOp",EDGE,"E282"),sQuery(id+"F20.wireOp",EDGE,"E283"),sQuery(id+"F20.wireOp",EDGE,"E284"),sQuery(id+"F20.wireOp",EDGE,"E285"),sQuery(id+"F20.wireOp",EDGE,"E286"),sQuery(id+"F20.wireOp",EDGE,"E287.trimOffspring"),sQuery(id+"F20.wireOp",EDGE,"E288.trimOffspring"),sQuery(id+"F20.wireOp",EDGE,"E289.trimOffspring"),sQuery(id+"F20.wireOp",EDGE,"E290.trimOffspring"),sQuery(id+"F20.wireOp",EDGE,"E291.trimOffspring"),sQuery(id+"F20.wireOp",EDGE,"E292.trimOffspring"),sQuery(id+"F20.wireOp",EDGE,"E293.trimOffspring"),sQuery(id+"F20.wireOp",EDGE,"E294.trimOffspring")])]}),"instanceName":"1"}),"instanceName":"1"}),"instanceName":"1"}),"instanceName":"1"}),"instanceName":"1"}),"instanceName":"1"}),"instanceName":"1"}),"instanceName":"1"});
            var Q8;
            Q8=makeQuery(id+"F29.opPattern","COPY",BODY,{"derivedFrom":makeQuery(id+"F28.opPattern","COPY",BODY,{"derivedFrom":makeQuery(id+"F27.opPattern","COPY",BODY,{"derivedFrom":makeQuery(id+"F26.opPattern","COPY",BODY,{"derivedFrom":makeQuery(id+"F25.opPattern","COPY",BODY,{"derivedFrom":makeQuery(id+"F24.opPattern","COPY",BODY,{"derivedFrom":makeQuery(id+"F23.opPattern","COPY",BODY,{"derivedFrom":makeQuery(id+"F21.opExtrude","SWEPT_BODY",BODY,{"disambiguationData":[OSD([sQuery(id+"F20.wireOp",EDGE,"E271"),sQuery(id+"F20.wireOp",EDGE,"E272"),sQuery(id+"F20.wireOp",EDGE,"E273"),sQuery(id+"F20.wireOp",EDGE,"E274"),sQuery(id+"F20.wireOp",EDGE,"E275"),sQuery(id+"F20.wireOp",EDGE,"E276"),sQuery(id+"F20.wireOp",EDGE,"E277"),sQuery(id+"F20.wireOp",EDGE,"E278"),sQuery(id+"F20.wireOp",EDGE,"E279"),sQuery(id+"F20.wireOp",EDGE,"E280"),sQuery(id+"F20.wireOp",EDGE,"E281"),sQuery(id+"F20.wireOp",EDGE,"E282"),sQuery(id+"F20.wireOp",EDGE,"E283"),sQuery(id+"F20.wireOp",EDGE,"E284"),sQuery(id+"F20.wireOp",EDGE,"E285"),sQuery(id+"F20.wireOp",EDGE,"E286"),sQuery(id+"F20.wireOp",EDGE,"E287.trimOffspring"),sQuery(id+"F20.wireOp",EDGE,"E288.trimOffspring"),sQuery(id+"F20.wireOp",EDGE,"E289.trimOffspring"),sQuery(id+"F20.wireOp",EDGE,"E290.trimOffspring"),sQuery(id+"F20.wireOp",EDGE,"E291.trimOffspring"),sQuery(id+"F20.wireOp",EDGE,"E292.trimOffspring"),sQuery(id+"F20.wireOp",EDGE,"E293.trimOffspring"),sQuery(id+"F20.wireOp",EDGE,"E294.trimOffspring")])]}),"instanceName":"1"}),"instanceName":"1"}),"instanceName":"1"}),"instanceName":"1"}),"instanceName":"1"}),"instanceName":"1"}),"instanceName":"1"});
            var Q9;
            Q9=makeQuery(id+"F28.opPattern","COPY",BODY,{"derivedFrom":makeQuery(id+"F27.opPattern","COPY",BODY,{"derivedFrom":makeQuery(id+"F26.opPattern","COPY",BODY,{"derivedFrom":makeQuery(id+"F25.opPattern","COPY",BODY,{"derivedFrom":makeQuery(id+"F24.opPattern","COPY",BODY,{"derivedFrom":makeQuery(id+"F23.opPattern","COPY",BODY,{"derivedFrom":makeQuery(id+"F21.opExtrude","SWEPT_BODY",BODY,{"disambiguationData":[OSD([sQuery(id+"F20.wireOp",EDGE,"E271"),sQuery(id+"F20.wireOp",EDGE,"E272"),sQuery(id+"F20.wireOp",EDGE,"E273"),sQuery(id+"F20.wireOp",EDGE,"E274"),sQuery(id+"F20.wireOp",EDGE,"E275"),sQuery(id+"F20.wireOp",EDGE,"E276"),sQuery(id+"F20.wireOp",EDGE,"E277"),sQuery(id+"F20.wireOp",EDGE,"E278"),sQuery(id+"F20.wireOp",EDGE,"E279"),sQuery(id+"F20.wireOp",EDGE,"E280"),sQuery(id+"F20.wireOp",EDGE,"E281"),sQuery(id+"F20.wireOp",EDGE,"E282"),sQuery(id+"F20.wireOp",EDGE,"E283"),sQuery(id+"F20.wireOp",EDGE,"E284"),sQuery(id+"F20.wireOp",EDGE,"E285"),sQuery(id+"F20.wireOp",EDGE,"E286"),sQuery(id+"F20.wireOp",EDGE,"E287.trimOffspring"),sQuery(id+"F20.wireOp",EDGE,"E288.trimOffspring"),sQuery(id+"F20.wireOp",EDGE,"E289.trimOffspring"),sQuery(id+"F20.wireOp",EDGE,"E290.trimOffspring"),sQuery(id+"F20.wireOp",EDGE,"E291.trimOffspring"),sQuery(id+"F20.wireOp",EDGE,"E292.trimOffspring"),sQuery(id+"F20.wireOp",EDGE,"E293.trimOffspring"),sQuery(id+"F20.wireOp",EDGE,"E294.trimOffspring")])]}),"instanceName":"1"}),"instanceName":"1"}),"instanceName":"1"}),"instanceName":"1"}),"instanceName":"1"}),"instanceName":"1"});
            var Q10;
            Q10=makeQuery(id+"F27.opPattern","COPY",BODY,{"derivedFrom":makeQuery(id+"F26.opPattern","COPY",BODY,{"derivedFrom":makeQuery(id+"F25.opPattern","COPY",BODY,{"derivedFrom":makeQuery(id+"F24.opPattern","COPY",BODY,{"derivedFrom":makeQuery(id+"F23.opPattern","COPY",BODY,{"derivedFrom":makeQuery(id+"F21.opExtrude","SWEPT_BODY",BODY,{"disambiguationData":[OSD([sQuery(id+"F20.wireOp",EDGE,"E271"),sQuery(id+"F20.wireOp",EDGE,"E272"),sQuery(id+"F20.wireOp",EDGE,"E273"),sQuery(id+"F20.wireOp",EDGE,"E274"),sQuery(id+"F20.wireOp",EDGE,"E275"),sQuery(id+"F20.wireOp",EDGE,"E276"),sQuery(id+"F20.wireOp",EDGE,"E277"),sQuery(id+"F20.wireOp",EDGE,"E278"),sQuery(id+"F20.wireOp",EDGE,"E279"),sQuery(id+"F20.wireOp",EDGE,"E280"),sQuery(id+"F20.wireOp",EDGE,"E281"),sQuery(id+"F20.wireOp",EDGE,"E282"),sQuery(id+"F20.wireOp",EDGE,"E283"),sQuery(id+"F20.wireOp",EDGE,"E284"),sQuery(id+"F20.wireOp",EDGE,"E285"),sQuery(id+"F20.wireOp",EDGE,"E286"),sQuery(id+"F20.wireOp",EDGE,"E287.trimOffspring"),sQuery(id+"F20.wireOp",EDGE,"E288.trimOffspring"),sQuery(id+"F20.wireOp",EDGE,"E289.trimOffspring"),sQuery(id+"F20.wireOp",EDGE,"E290.trimOffspring"),sQuery(id+"F20.wireOp",EDGE,"E291.trimOffspring"),sQuery(id+"F20.wireOp",EDGE,"E292.trimOffspring"),sQuery(id+"F20.wireOp",EDGE,"E293.trimOffspring"),sQuery(id+"F20.wireOp",EDGE,"E294.trimOffspring")])]}),"instanceName":"1"}),"instanceName":"1"}),"instanceName":"1"}),"instanceName":"1"}),"instanceName":"1"});
            var Q11;
            Q11=makeQuery(id+"F26.opPattern","COPY",BODY,{"derivedFrom":makeQuery(id+"F25.opPattern","COPY",BODY,{"derivedFrom":makeQuery(id+"F24.opPattern","COPY",BODY,{"derivedFrom":makeQuery(id+"F23.opPattern","COPY",BODY,{"derivedFrom":makeQuery(id+"F21.opExtrude","SWEPT_BODY",BODY,{"disambiguationData":[OSD([sQuery(id+"F20.wireOp",EDGE,"E271"),sQuery(id+"F20.wireOp",EDGE,"E272"),sQuery(id+"F20.wireOp",EDGE,"E273"),sQuery(id+"F20.wireOp",EDGE,"E274"),sQuery(id+"F20.wireOp",EDGE,"E275"),sQuery(id+"F20.wireOp",EDGE,"E276"),sQuery(id+"F20.wireOp",EDGE,"E277"),sQuery(id+"F20.wireOp",EDGE,"E278"),sQuery(id+"F20.wireOp",EDGE,"E279"),sQuery(id+"F20.wireOp",EDGE,"E280"),sQuery(id+"F20.wireOp",EDGE,"E281"),sQuery(id+"F20.wireOp",EDGE,"E282"),sQuery(id+"F20.wireOp",EDGE,"E283"),sQuery(id+"F20.wireOp",EDGE,"E284"),sQuery(id+"F20.wireOp",EDGE,"E285"),sQuery(id+"F20.wireOp",EDGE,"E286"),sQuery(id+"F20.wireOp",EDGE,"E287.trimOffspring"),sQuery(id+"F20.wireOp",EDGE,"E288.trimOffspring"),sQuery(id+"F20.wireOp",EDGE,"E289.trimOffspring"),sQuery(id+"F20.wireOp",EDGE,"E290.trimOffspring"),sQuery(id+"F20.wireOp",EDGE,"E291.trimOffspring"),sQuery(id+"F20.wireOp",EDGE,"E292.trimOffspring"),sQuery(id+"F20.wireOp",EDGE,"E293.trimOffspring"),sQuery(id+"F20.wireOp",EDGE,"E294.trimOffspring")])]}),"instanceName":"1"}),"instanceName":"1"}),"instanceName":"1"}),"instanceName":"1"});
            var Q12;
            Q12=makeQuery(id+"F25.opPattern","COPY",BODY,{"derivedFrom":makeQuery(id+"F24.opPattern","COPY",BODY,{"derivedFrom":makeQuery(id+"F23.opPattern","COPY",BODY,{"derivedFrom":makeQuery(id+"F21.opExtrude","SWEPT_BODY",BODY,{"disambiguationData":[OSD([sQuery(id+"F20.wireOp",EDGE,"E271"),sQuery(id+"F20.wireOp",EDGE,"E272"),sQuery(id+"F20.wireOp",EDGE,"E273"),sQuery(id+"F20.wireOp",EDGE,"E274"),sQuery(id+"F20.wireOp",EDGE,"E275"),sQuery(id+"F20.wireOp",EDGE,"E276"),sQuery(id+"F20.wireOp",EDGE,"E277"),sQuery(id+"F20.wireOp",EDGE,"E278"),sQuery(id+"F20.wireOp",EDGE,"E279"),sQuery(id+"F20.wireOp",EDGE,"E280"),sQuery(id+"F20.wireOp",EDGE,"E281"),sQuery(id+"F20.wireOp",EDGE,"E282"),sQuery(id+"F20.wireOp",EDGE,"E283"),sQuery(id+"F20.wireOp",EDGE,"E284"),sQuery(id+"F20.wireOp",EDGE,"E285"),sQuery(id+"F20.wireOp",EDGE,"E286"),sQuery(id+"F20.wireOp",EDGE,"E287.trimOffspring"),sQuery(id+"F20.wireOp",EDGE,"E288.trimOffspring"),sQuery(id+"F20.wireOp",EDGE,"E289.trimOffspring"),sQuery(id+"F20.wireOp",EDGE,"E290.trimOffspring"),sQuery(id+"F20.wireOp",EDGE,"E291.trimOffspring"),sQuery(id+"F20.wireOp",EDGE,"E292.trimOffspring"),sQuery(id+"F20.wireOp",EDGE,"E293.trimOffspring"),sQuery(id+"F20.wireOp",EDGE,"E294.trimOffspring")])]}),"instanceName":"1"}),"instanceName":"1"}),"instanceName":"1"});
            var Q13;
            Q13=makeQuery(id+"F24.opPattern","COPY",BODY,{"derivedFrom":makeQuery(id+"F23.opPattern","COPY",BODY,{"derivedFrom":makeQuery(id+"F21.opExtrude","SWEPT_BODY",BODY,{"disambiguationData":[OSD([sQuery(id+"F20.wireOp",EDGE,"E271"),sQuery(id+"F20.wireOp",EDGE,"E272"),sQuery(id+"F20.wireOp",EDGE,"E273"),sQuery(id+"F20.wireOp",EDGE,"E274"),sQuery(id+"F20.wireOp",EDGE,"E275"),sQuery(id+"F20.wireOp",EDGE,"E276"),sQuery(id+"F20.wireOp",EDGE,"E277"),sQuery(id+"F20.wireOp",EDGE,"E278"),sQuery(id+"F20.wireOp",EDGE,"E279"),sQuery(id+"F20.wireOp",EDGE,"E280"),sQuery(id+"F20.wireOp",EDGE,"E281"),sQuery(id+"F20.wireOp",EDGE,"E282"),sQuery(id+"F20.wireOp",EDGE,"E283"),sQuery(id+"F20.wireOp",EDGE,"E284"),sQuery(id+"F20.wireOp",EDGE,"E285"),sQuery(id+"F20.wireOp",EDGE,"E286"),sQuery(id+"F20.wireOp",EDGE,"E287.trimOffspring"),sQuery(id+"F20.wireOp",EDGE,"E288.trimOffspring"),sQuery(id+"F20.wireOp",EDGE,"E289.trimOffspring"),sQuery(id+"F20.wireOp",EDGE,"E290.trimOffspring"),sQuery(id+"F20.wireOp",EDGE,"E291.trimOffspring"),sQuery(id+"F20.wireOp",EDGE,"E292.trimOffspring"),sQuery(id+"F20.wireOp",EDGE,"E293.trimOffspring"),sQuery(id+"F20.wireOp",EDGE,"E294.trimOffspring")])]}),"instanceName":"1"}),"instanceName":"1"});
            var Q14;
            Q14=makeQuery(id+"F23.opPattern","COPY",BODY,{"derivedFrom":makeQuery(id+"F21.opExtrude","SWEPT_BODY",BODY,{"disambiguationData":[OSD([sQuery(id+"F20.wireOp",EDGE,"E271"),sQuery(id+"F20.wireOp",EDGE,"E272"),sQuery(id+"F20.wireOp",EDGE,"E273"),sQuery(id+"F20.wireOp",EDGE,"E274"),sQuery(id+"F20.wireOp",EDGE,"E275"),sQuery(id+"F20.wireOp",EDGE,"E276"),sQuery(id+"F20.wireOp",EDGE,"E277"),sQuery(id+"F20.wireOp",EDGE,"E278"),sQuery(id+"F20.wireOp",EDGE,"E279"),sQuery(id+"F20.wireOp",EDGE,"E280"),sQuery(id+"F20.wireOp",EDGE,"E281"),sQuery(id+"F20.wireOp",EDGE,"E282"),sQuery(id+"F20.wireOp",EDGE,"E283"),sQuery(id+"F20.wireOp",EDGE,"E284"),sQuery(id+"F20.wireOp",EDGE,"E285"),sQuery(id+"F20.wireOp",EDGE,"E286"),sQuery(id+"F20.wireOp",EDGE,"E287.trimOffspring"),sQuery(id+"F20.wireOp",EDGE,"E288.trimOffspring"),sQuery(id+"F20.wireOp",EDGE,"E289.trimOffspring"),sQuery(id+"F20.wireOp",EDGE,"E290.trimOffspring"),sQuery(id+"F20.wireOp",EDGE,"E291.trimOffspring"),sQuery(id+"F20.wireOp",EDGE,"E292.trimOffspring"),sQuery(id+"F20.wireOp",EDGE,"E293.trimOffspring"),sQuery(id+"F20.wireOp",EDGE,"E294.trimOffspring")])]}),"instanceName":"1"});
            var Q15;
            Q15=makeQuery(id+"F22.opPattern","COPY",BODY,{"derivedFrom":makeQuery(id+"F21.opExtrude","SWEPT_BODY",BODY,{"disambiguationData":[OSD([sQuery(id+"F20.wireOp",EDGE,"E271"),sQuery(id+"F20.wireOp",EDGE,"E272"),sQuery(id+"F20.wireOp",EDGE,"E273"),sQuery(id+"F20.wireOp",EDGE,"E274"),sQuery(id+"F20.wireOp",EDGE,"E275"),sQuery(id+"F20.wireOp",EDGE,"E276"),sQuery(id+"F20.wireOp",EDGE,"E277"),sQuery(id+"F20.wireOp",EDGE,"E278"),sQuery(id+"F20.wireOp",EDGE,"E279"),sQuery(id+"F20.wireOp",EDGE,"E280"),sQuery(id+"F20.wireOp",EDGE,"E281"),sQuery(id+"F20.wireOp",EDGE,"E282"),sQuery(id+"F20.wireOp",EDGE,"E283"),sQuery(id+"F20.wireOp",EDGE,"E284"),sQuery(id+"F20.wireOp",EDGE,"E285"),sQuery(id+"F20.wireOp",EDGE,"E286"),sQuery(id+"F20.wireOp",EDGE,"E287.trimOffspring"),sQuery(id+"F20.wireOp",EDGE,"E288.trimOffspring"),sQuery(id+"F20.wireOp",EDGE,"E289.trimOffspring"),sQuery(id+"F20.wireOp",EDGE,"E290.trimOffspring"),sQuery(id+"F20.wireOp",EDGE,"E291.trimOffspring"),sQuery(id+"F20.wireOp",EDGE,"E292.trimOffspring"),sQuery(id+"F20.wireOp",EDGE,"E293.trimOffspring"),sQuery(id+"F20.wireOp",EDGE,"E294.trimOffspring")])]}),"instanceName":"1"});
            var Q16;
            Q16=makeQuery(id+"F21.opExtrude","SWEPT_BODY",BODY,{"disambiguationData":[OSD([sQuery(id+"F20.wireOp",EDGE,"E271"),sQuery(id+"F20.wireOp",EDGE,"E272"),sQuery(id+"F20.wireOp",EDGE,"E273"),sQuery(id+"F20.wireOp",EDGE,"E274"),sQuery(id+"F20.wireOp",EDGE,"E275"),sQuery(id+"F20.wireOp",EDGE,"E276"),sQuery(id+"F20.wireOp",EDGE,"E277"),sQuery(id+"F20.wireOp",EDGE,"E278"),sQuery(id+"F20.wireOp",EDGE,"E279"),sQuery(id+"F20.wireOp",EDGE,"E280"),sQuery(id+"F20.wireOp",EDGE,"E281"),sQuery(id+"F20.wireOp",EDGE,"E282"),sQuery(id+"F20.wireOp",EDGE,"E283"),sQuery(id+"F20.wireOp",EDGE,"E284"),sQuery(id+"F20.wireOp",EDGE,"E285"),sQuery(id+"F20.wireOp",EDGE,"E286"),sQuery(id+"F20.wireOp",EDGE,"E287.trimOffspring"),sQuery(id+"F20.wireOp",EDGE,"E288.trimOffspring"),sQuery(id+"F20.wireOp",EDGE,"E289.trimOffspring"),sQuery(id+"F20.wireOp",EDGE,"E290.trimOffspring"),sQuery(id+"F20.wireOp",EDGE,"E291.trimOffspring"),sQuery(id+"F20.wireOp",EDGE,"E292.trimOffspring"),sQuery(id+"F20.wireOp",EDGE,"E293.trimOffspring"),sQuery(id+"F20.wireOp",EDGE,"E294.trimOffspring")])]});
            var Q17;
            Q17=makeQuery(id+"F1.opExtrude","SWEPT_BODY",BODY,{"disambiguationData":[OSD([sQuery(id+"F0.wireOp",EDGE,"E0")])]});
            booleanBodies(context, id + "F38", {"operationType" : BooleanOperationType.SUBTRACTION, "tools" : qUnion([Q0, Q1, Q2, Q3, Q4, Q5, Q6, Q7, Q8, Q9, Q10, Q11, Q12, Q13, Q14, Q15, Q16]), "targets" : qUnion([Q17])});
        }
    });
